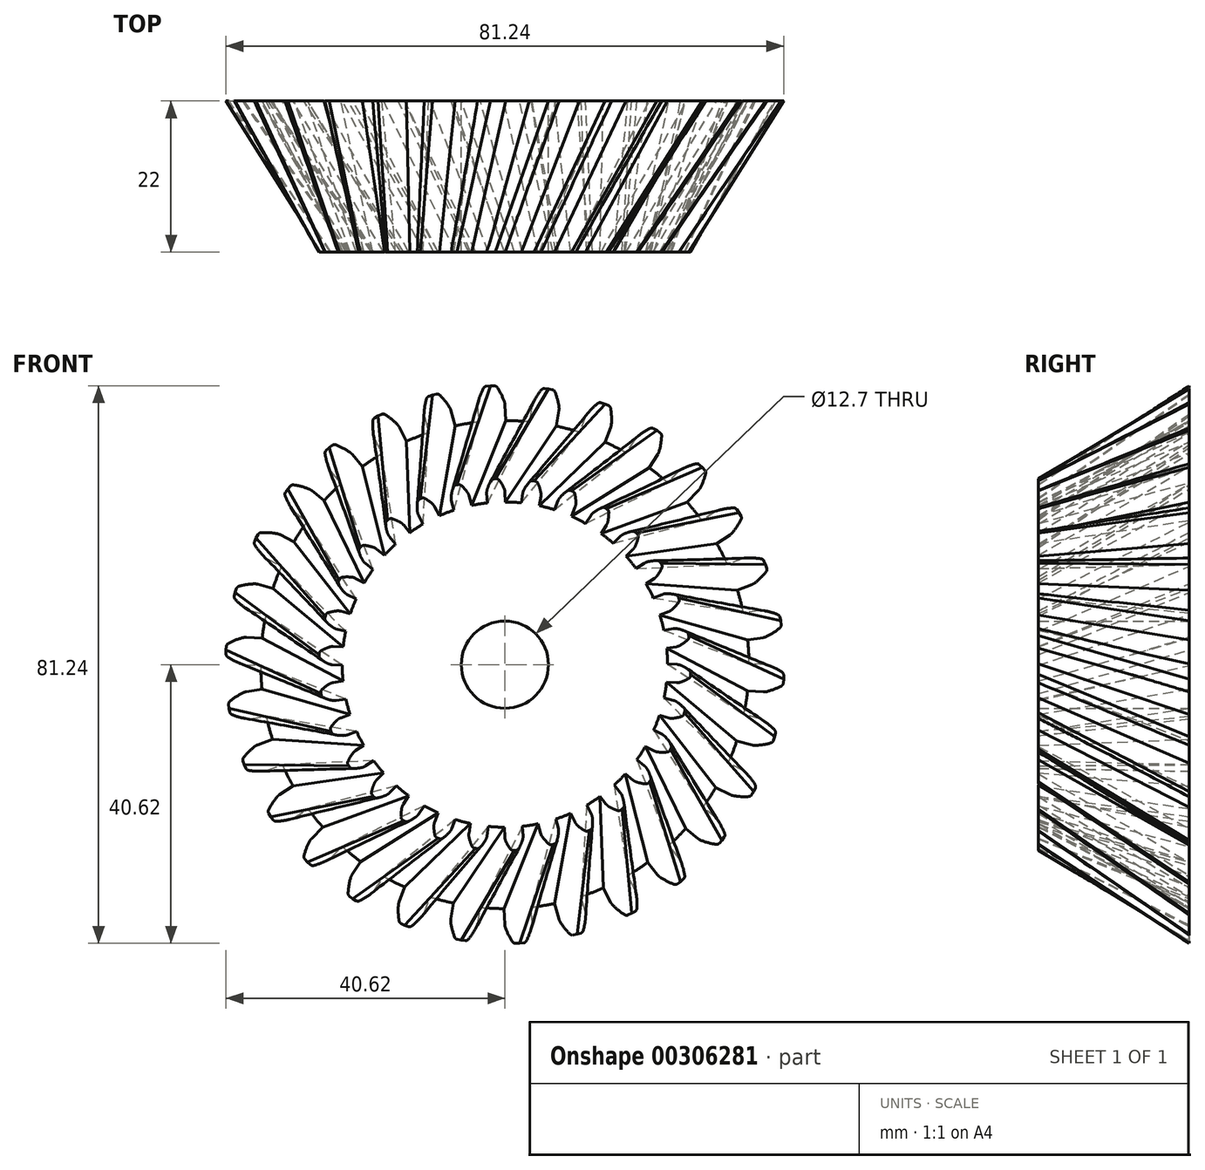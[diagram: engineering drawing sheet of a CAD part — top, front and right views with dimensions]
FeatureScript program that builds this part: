
annotation { "Feature Type Name" : "Feature", "Feature Type Description" : "" }
export const myFeature = defineFeature(function(context is Context, id is Id, definition is map)
    precondition{}
    {
        {
            var Q0;
            Q0=qCreatedBy(makeId("Front.planeOp"),FACE);
            cPlane(context, id + "F0", {"entities" : qUnion([Q0]), "cplaneType" : CPlaneType.OFFSET, "offset" : 22 * mm, "width" : 152.4 * mm, "height" : 152.4 * mm});
        }
        {
            var Q0;
            Q0=qCreatedBy(makeId("Front.planeOp"),FACE);
            var sketch = newSketch(context, id + "F1", { "sketchPlane" : qUnion([Q0])});
            skArc(sketch, "E0", {"start": v(-3.85, 35.35) * mm, "mid": v(-5.56, 35.12) * mm, "end": v(-7.26, 34.81) * mm});
            skArc(sketch, "E1.trimOffspring", {"start": v(-0.08, 38.33) * mm, "mid": v(-0.54, 39.4) * mm, "end": v(-1.12, 40.4) * mm});
            skLineSegment(sketch, "E2", {"start": v(-1.54, 40.62) * mm, "end": v(-2.13, 40.62) * mm});
            skLineSegment(sketch, "E3", {"start": v(0.01, 37.88) * mm, "end": v(0.13, 35.56) * mm});
            skLineSegment(sketch, "E4.MirrorCS", {"start": v(-2.7, 40.56) * mm, "end": v(-2.13, 40.62) * mm});
            skArc(sketch, "E5.MirrorCS", {"start": v(-3.93, 38.13) * mm, "mid": v(-3.58, 39.24) * mm, "end": v(-3.1, 40.3) * mm});
            skLineSegment(sketch, "E6.MirrorCS", {"start": v(-3.97, 37.67) * mm, "end": v(-3.85, 35.35) * mm});
            skPoint(sketch, "E7.visualSharp", {"position": v(-2.98, 40.53) * mm});
            skArc(sketch, "E7.filletArc", {"start": v(-2.7, 40.56) * mm, "mid": v(-2.94, 40.47) * mm, "end": v(-3.1, 40.3) * mm});
            skPoint(sketch, "E8.visualSharp", {"position": v(-1.28, 40.62) * mm});
            skArc(sketch, "E8.filletArc", {"start": v(-1.12, 40.4) * mm, "mid": v(-1.3, 40.56) * mm, "end": v(-1.54, 40.62) * mm});
            skPoint(sketch, "E9.visualSharp", {"position": v(-3.98, 37.9) * mm});
            skArc(sketch, "E9.filletArc", {"start": v(-3.93, 38.13) * mm, "mid": v(-3.97, 37.9) * mm, "end": v(-3.97, 37.67) * mm});
            skPoint(sketch, "E10.visualSharp", {"position": v(0, 38.1) * mm});
            skArc(sketch, "E10.filletArc", {"start": v(0.01, 37.88) * mm, "mid": v(-0.02, 38.1) * mm, "end": v(-0.08, 38.33) * mm});
            skLineSegment(sketch, "E11.1.0", {"start": v(-11.72, 36.02) * mm, "end": v(-11.12, 33.78) * mm});
            skPoint(sketch, "E11.1.1", {"position": v(-11.77, 36.24) * mm});
            skArc(sketch, "E11.1.2", {"start": v(-8.05, 37.48) * mm, "mid": v(-8.72, 38.42) * mm, "end": v(-9.5, 39.28) * mm});
            skArc(sketch, "E11.1.3", {"start": v(-11.77, 36.48) * mm, "mid": v(-11.66, 37.63) * mm, "end": v(-11.42, 38.76) * mm});
            skLineSegment(sketch, "E11.1.4", {"start": v(-9.96, 39.41) * mm, "end": v(-10.53, 39.29) * mm});
            skPoint(sketch, "E11.1.5", {"position": v(-11.34, 39.03) * mm});
            skPoint(sketch, "E11.1.6", {"position": v(-9.7, 39.47) * mm});
            skPoint(sketch, "E11.1.7", {"position": v(-7.92, 37.27) * mm});
            skLineSegment(sketch, "E11.1.8", {"start": v(-7.86, 37.05) * mm, "end": v(-7.26, 34.81) * mm});
            skLineSegment(sketch, "E11.1.9", {"start": v(-11.08, 39.1) * mm, "end": v(-10.53, 39.29) * mm});
            skArc(sketch, "E11.1.10", {"start": v(-11.08, 39.1) * mm, "mid": v(-11.3, 38.98) * mm, "end": v(-11.42, 38.76) * mm});
            skArc(sketch, "E11.1.11", {"start": v(-9.5, 39.28) * mm, "mid": v(-9.7, 39.4) * mm, "end": v(-9.96, 39.41) * mm});
            skArc(sketch, "E11.1.12", {"start": v(-11.77, 36.48) * mm, "mid": v(-11.76, 36.25) * mm, "end": v(-11.72, 36.02) * mm});
            skArc(sketch, "E11.1.13", {"start": v(-7.86, 37.05) * mm, "mid": v(-7.94, 37.27) * mm, "end": v(-8.05, 37.48) * mm});
            skLineSegment(sketch, "E11.2.0", {"start": v(-18.95, 32.8) * mm, "end": v(-17.9, 30.73) * mm});
            skPoint(sketch, "E11.2.1", {"position": v(-19.05, 33) * mm});
            skArc(sketch, "E11.2.2", {"start": v(-15.66, 34.99) * mm, "mid": v(-16.52, 35.77) * mm, "end": v(-17.45, 36.45) * mm});
            skArc(sketch, "E11.2.3", {"start": v(-19.1, 33.24) * mm, "mid": v(-19.23, 34.39) * mm, "end": v(-19.23, 35.54) * mm});
            skLineSegment(sketch, "E11.2.4", {"start": v(-17.93, 36.48) * mm, "end": v(-18.47, 36.24) * mm});
            skPoint(sketch, "E11.2.5", {"position": v(-19.2, 35.82) * mm});
            skPoint(sketch, "E11.2.6", {"position": v(-17.69, 36.59) * mm});
            skPoint(sketch, "E11.2.7", {"position": v(-15.5, 34.8) * mm});
            skLineSegment(sketch, "E11.2.8", {"start": v(-15.4, 34.6) * mm, "end": v(-14.34, 32.54) * mm});
            skLineSegment(sketch, "E11.2.9", {"start": v(-18.97, 35.95) * mm, "end": v(-18.47, 36.24) * mm});
            skArc(sketch, "E11.2.10", {"start": v(-18.97, 35.95) * mm, "mid": v(-19.15, 35.78) * mm, "end": v(-19.23, 35.54) * mm});
            skArc(sketch, "E11.2.11", {"start": v(-17.45, 36.45) * mm, "mid": v(-17.69, 36.52) * mm, "end": v(-17.93, 36.48) * mm});
            skArc(sketch, "E11.2.12", {"start": v(-19.1, 33.24) * mm, "mid": v(-19.04, 33.01) * mm, "end": v(-18.95, 32.8) * mm});
            skArc(sketch, "E11.2.13", {"start": v(-15.4, 34.6) * mm, "mid": v(-15.52, 34.8) * mm, "end": v(-15.66, 34.99) * mm});
            skLineSegment(sketch, "E11.3.0", {"start": v(-25.35, 28.14) * mm, "end": v(-23.9, 26.34) * mm});
            skPoint(sketch, "E11.3.1", {"position": v(-25.5, 28.31) * mm});
            skArc(sketch, "E11.3.2", {"start": v(-22.6, 30.96) * mm, "mid": v(-23.6, 31.55) * mm, "end": v(-24.65, 32.02) * mm});
            skArc(sketch, "E11.3.3", {"start": v(-25.59, 28.54) * mm, "mid": v(-25.96, 29.64) * mm, "end": v(-26.2, 30.77) * mm});
            skLineSegment(sketch, "E11.3.4", {"start": v(-25.13, 31.95) * mm, "end": v(-25.6, 31.61) * mm});
            skPoint(sketch, "E11.3.5", {"position": v(-26.23, 31.04) * mm});
            skPoint(sketch, "E11.3.6", {"position": v(-24.9, 32.11) * mm});
            skPoint(sketch, "E11.3.7", {"position": v(-22.4, 30.82) * mm});
            skLineSegment(sketch, "E11.3.8", {"start": v(-22.25, 30.65) * mm, "end": v(-20.8, 28.85) * mm});
            skLineSegment(sketch, "E11.3.9", {"start": v(-26.03, 31.22) * mm, "end": v(-25.6, 31.61) * mm});
            skArc(sketch, "E11.3.10", {"start": v(-26.03, 31.22) * mm, "mid": v(-26.17, 31.02) * mm, "end": v(-26.2, 30.77) * mm});
            skArc(sketch, "E11.3.11", {"start": v(-24.65, 32.02) * mm, "mid": v(-24.9, 32.05) * mm, "end": v(-25.13, 31.95) * mm});
            skArc(sketch, "E11.3.12", {"start": v(-25.59, 28.54) * mm, "mid": v(-25.49, 28.33) * mm, "end": v(-25.35, 28.14) * mm});
            skArc(sketch, "E11.3.13", {"start": v(-22.25, 30.65) * mm, "mid": v(-22.41, 30.82) * mm, "end": v(-22.6, 30.96) * mm});
            skLineSegment(sketch, "E11.4.0", {"start": v(-30.65, 22.25) * mm, "end": v(-28.85, 20.8) * mm});
            skPoint(sketch, "E11.4.1", {"position": v(-30.82, 22.4) * mm});
            skArc(sketch, "E11.4.2", {"start": v(-28.54, 25.59) * mm, "mid": v(-29.64, 25.96) * mm, "end": v(-30.77, 26.2) * mm});
            skArc(sketch, "E11.4.3", {"start": v(-30.96, 22.6) * mm, "mid": v(-31.55, 23.6) * mm, "end": v(-32.02, 24.65) * mm});
            skLineSegment(sketch, "E11.4.4", {"start": v(-31.22, 26.03) * mm, "end": v(-31.61, 25.6) * mm});
            skPoint(sketch, "E11.4.5", {"position": v(-32.11, 24.9) * mm});
            skPoint(sketch, "E11.4.6", {"position": v(-31.04, 26.23) * mm});
            skPoint(sketch, "E11.4.7", {"position": v(-28.31, 25.5) * mm});
            skLineSegment(sketch, "E11.4.8", {"start": v(-28.14, 25.35) * mm, "end": v(-26.34, 23.9) * mm});
            skLineSegment(sketch, "E11.4.9", {"start": v(-31.95, 25.13) * mm, "end": v(-31.61, 25.6) * mm});
            skArc(sketch, "E11.4.10", {"start": v(-31.95, 25.13) * mm, "mid": v(-32.05, 24.9) * mm, "end": v(-32.02, 24.65) * mm});
            skArc(sketch, "E11.4.11", {"start": v(-30.77, 26.2) * mm, "mid": v(-31.02, 26.17) * mm, "end": v(-31.22, 26.03) * mm});
            skArc(sketch, "E11.4.12", {"start": v(-30.96, 22.6) * mm, "mid": v(-30.82, 22.41) * mm, "end": v(-30.65, 22.25) * mm});
            skArc(sketch, "E11.4.13", {"start": v(-28.14, 25.35) * mm, "mid": v(-28.33, 25.49) * mm, "end": v(-28.54, 25.59) * mm});
            skLineSegment(sketch, "E11.5.0", {"start": v(-34.6, 15.4) * mm, "end": v(-32.54, 14.34) * mm});
            skPoint(sketch, "E11.5.1", {"position": v(-34.8, 15.5) * mm});
            skArc(sketch, "E11.5.2", {"start": v(-33.24, 19.1) * mm, "mid": v(-34.39, 19.23) * mm, "end": v(-35.54, 19.23) * mm});
            skArc(sketch, "E11.5.3", {"start": v(-34.99, 15.66) * mm, "mid": v(-35.77, 16.52) * mm, "end": v(-36.45, 17.45) * mm});
            skLineSegment(sketch, "E11.5.4", {"start": v(-35.95, 18.97) * mm, "end": v(-36.24, 18.47) * mm});
            skPoint(sketch, "E11.5.5", {"position": v(-36.59, 17.69) * mm});
            skPoint(sketch, "E11.5.6", {"position": v(-35.82, 19.2) * mm});
            skPoint(sketch, "E11.5.7", {"position": v(-33, 19.05) * mm});
            skLineSegment(sketch, "E11.5.8", {"start": v(-32.8, 18.95) * mm, "end": v(-30.73, 17.9) * mm});
            skLineSegment(sketch, "E11.5.9", {"start": v(-36.48, 17.93) * mm, "end": v(-36.24, 18.47) * mm});
            skArc(sketch, "E11.5.10", {"start": v(-36.48, 17.93) * mm, "mid": v(-36.52, 17.69) * mm, "end": v(-36.45, 17.45) * mm});
            skArc(sketch, "E11.5.11", {"start": v(-35.54, 19.23) * mm, "mid": v(-35.78, 19.15) * mm, "end": v(-35.95, 18.97) * mm});
            skArc(sketch, "E11.5.12", {"start": v(-34.99, 15.66) * mm, "mid": v(-34.8, 15.52) * mm, "end": v(-34.6, 15.4) * mm});
            skArc(sketch, "E11.5.13", {"start": v(-32.8, 18.95) * mm, "mid": v(-33.01, 19.04) * mm, "end": v(-33.24, 19.1) * mm});
            skLineSegment(sketch, "E11.6.0", {"start": v(-37.05, 7.86) * mm, "end": v(-34.81, 7.26) * mm});
            skPoint(sketch, "E11.6.1", {"position": v(-37.27, 7.92) * mm});
            skArc(sketch, "E11.6.2", {"start": v(-36.48, 11.77) * mm, "mid": v(-37.63, 11.66) * mm, "end": v(-38.76, 11.42) * mm});
            skArc(sketch, "E11.6.3", {"start": v(-37.48, 8.05) * mm, "mid": v(-38.42, 8.72) * mm, "end": v(-39.28, 9.5) * mm});
            skLineSegment(sketch, "E11.6.4", {"start": v(-39.1, 11.08) * mm, "end": v(-39.29, 10.53) * mm});
            skPoint(sketch, "E11.6.5", {"position": v(-39.47, 9.7) * mm});
            skPoint(sketch, "E11.6.6", {"position": v(-39.03, 11.34) * mm});
            skPoint(sketch, "E11.6.7", {"position": v(-36.24, 11.77) * mm});
            skLineSegment(sketch, "E11.6.8", {"start": v(-36.02, 11.72) * mm, "end": v(-33.78, 11.12) * mm});
            skLineSegment(sketch, "E11.6.9", {"start": v(-39.41, 9.96) * mm, "end": v(-39.29, 10.53) * mm});
            skArc(sketch, "E11.6.10", {"start": v(-39.41, 9.96) * mm, "mid": v(-39.4, 9.7) * mm, "end": v(-39.28, 9.5) * mm});
            skArc(sketch, "E11.6.11", {"start": v(-38.76, 11.42) * mm, "mid": v(-38.98, 11.3) * mm, "end": v(-39.1, 11.08) * mm});
            skArc(sketch, "E11.6.12", {"start": v(-37.48, 8.05) * mm, "mid": v(-37.27, 7.94) * mm, "end": v(-37.05, 7.86) * mm});
            skArc(sketch, "E11.6.13", {"start": v(-36.02, 11.72) * mm, "mid": v(-36.25, 11.76) * mm, "end": v(-36.48, 11.77) * mm});
            skLineSegment(sketch, "E11.7.0", {"start": v(-37.88, -0.01) * mm, "end": v(-35.56, -0.13) * mm});
            skPoint(sketch, "E11.7.1", {"position": v(-38.1, 0) * mm});
            skArc(sketch, "E11.7.2", {"start": v(-38.13, 3.93) * mm, "mid": v(-39.24, 3.58) * mm, "end": v(-40.3, 3.1) * mm});
            skArc(sketch, "E11.7.3", {"start": v(-38.33, 0.08) * mm, "mid": v(-39.4, 0.54) * mm, "end": v(-40.4, 1.12) * mm});
            skLineSegment(sketch, "E11.7.4", {"start": v(-40.56, 2.7) * mm, "end": v(-40.62, 2.13) * mm});
            skPoint(sketch, "E11.7.5", {"position": v(-40.62, 1.28) * mm});
            skPoint(sketch, "E11.7.6", {"position": v(-40.53, 2.98) * mm});
            skPoint(sketch, "E11.7.7", {"position": v(-37.9, 3.98) * mm});
            skLineSegment(sketch, "E11.7.8", {"start": v(-37.67, 3.97) * mm, "end": v(-35.35, 3.85) * mm});
            skLineSegment(sketch, "E11.7.9", {"start": v(-40.62, 1.54) * mm, "end": v(-40.62, 2.13) * mm});
            skArc(sketch, "E11.7.10", {"start": v(-40.62, 1.54) * mm, "mid": v(-40.56, 1.3) * mm, "end": v(-40.4, 1.12) * mm});
            skArc(sketch, "E11.7.11", {"start": v(-40.3, 3.1) * mm, "mid": v(-40.47, 2.94) * mm, "end": v(-40.56, 2.7) * mm});
            skArc(sketch, "E11.7.12", {"start": v(-38.33, 0.08) * mm, "mid": v(-38.1, 0.02) * mm, "end": v(-37.88, -0.01) * mm});
            skArc(sketch, "E11.7.13", {"start": v(-37.67, 3.97) * mm, "mid": v(-37.9, 3.97) * mm, "end": v(-38.13, 3.93) * mm});
            skLineSegment(sketch, "E11.8.0", {"start": v(-37.05, -7.89) * mm, "end": v(-34.76, -7.52) * mm});
            skPoint(sketch, "E11.8.1", {"position": v(-37.27, -7.92) * mm});
            skArc(sketch, "E11.8.2", {"start": v(-38.11, -4.09) * mm, "mid": v(-39.12, -4.65) * mm, "end": v(-40.06, -5.34) * mm});
            skArc(sketch, "E11.8.3", {"start": v(-37.51, -7.9) * mm, "mid": v(-38.65, -7.66) * mm, "end": v(-39.74, -7.3) * mm});
            skLineSegment(sketch, "E11.8.4", {"start": v(-40.24, -5.78) * mm, "end": v(-40.17, -6.36) * mm});
            skPoint(sketch, "E11.8.5", {"position": v(-40, -7.2) * mm});
            skPoint(sketch, "E11.8.6", {"position": v(-40.26, -5.52) * mm});
            skPoint(sketch, "E11.8.7", {"position": v(-37.9, -3.98) * mm});
            skLineSegment(sketch, "E11.8.8", {"start": v(-37.67, -3.95) * mm, "end": v(-35.38, -3.58) * mm});
            skLineSegment(sketch, "E11.8.9", {"start": v(-40.05, -6.93) * mm, "end": v(-40.17, -6.36) * mm});
            skArc(sketch, "E11.8.10", {"start": v(-40.05, -6.93) * mm, "mid": v(-39.94, -7.16) * mm, "end": v(-39.74, -7.3) * mm});
            skArc(sketch, "E11.8.11", {"start": v(-40.06, -5.34) * mm, "mid": v(-40.2, -5.54) * mm, "end": v(-40.24, -5.78) * mm});
            skArc(sketch, "E11.8.12", {"start": v(-37.51, -7.9) * mm, "mid": v(-37.28, -7.9) * mm, "end": v(-37.05, -7.89) * mm});
            skArc(sketch, "E11.8.13", {"start": v(-37.67, -3.95) * mm, "mid": v(-37.9, -4) * mm, "end": v(-38.11, -4.09) * mm});
            skLineSegment(sketch, "E11.9.0", {"start": v(-34.6, -15.42) * mm, "end": v(-32.43, -14.59) * mm});
            skPoint(sketch, "E11.9.1", {"position": v(-34.8, -15.5) * mm});
            skArc(sketch, "E11.9.2", {"start": v(-36.43, -11.92) * mm, "mid": v(-37.3, -12.69) * mm, "end": v(-38.07, -13.55) * mm});
            skArc(sketch, "E11.9.3", {"start": v(-35.05, -15.52) * mm, "mid": v(-36.2, -15.53) * mm, "end": v(-37.36, -15.4) * mm});
            skLineSegment(sketch, "E11.9.4", {"start": v(-38.15, -14.02) * mm, "end": v(-37.97, -14.58) * mm});
            skPoint(sketch, "E11.9.5", {"position": v(-37.63, -15.35) * mm});
            skPoint(sketch, "E11.9.6", {"position": v(-38.24, -13.77) * mm});
            skPoint(sketch, "E11.9.7", {"position": v(-36.24, -11.77) * mm});
            skLineSegment(sketch, "E11.9.8", {"start": v(-36.03, -11.7) * mm, "end": v(-33.86, -10.86) * mm});
            skLineSegment(sketch, "E11.9.9", {"start": v(-37.74, -15.11) * mm, "end": v(-37.97, -14.58) * mm});
            skArc(sketch, "E11.9.10", {"start": v(-37.74, -15.11) * mm, "mid": v(-37.58, -15.3) * mm, "end": v(-37.36, -15.4) * mm});
            skArc(sketch, "E11.9.11", {"start": v(-38.07, -13.55) * mm, "mid": v(-38.17, -13.77) * mm, "end": v(-38.15, -14.02) * mm});
            skArc(sketch, "E11.9.12", {"start": v(-35.05, -15.52) * mm, "mid": v(-34.82, -15.48) * mm, "end": v(-34.6, -15.42) * mm});
            skArc(sketch, "E11.9.13", {"start": v(-36.03, -11.7) * mm, "mid": v(-36.24, -11.8) * mm, "end": v(-36.43, -11.92) * mm});
            skLineSegment(sketch, "E11.10.0", {"start": v(-30.64, -22.27) * mm, "end": v(-28.7, -21) * mm});
            skPoint(sketch, "E11.10.1", {"position": v(-30.82, -22.4) * mm});
            skArc(sketch, "E11.10.2", {"start": v(-33.16, -19.24) * mm, "mid": v(-33.85, -20.16) * mm, "end": v(-34.42, -21.17) * mm});
            skArc(sketch, "E11.10.3", {"start": v(-31.06, -22.47) * mm, "mid": v(-32.19, -22.72) * mm, "end": v(-33.34, -22.84) * mm});
            skLineSegment(sketch, "E11.10.4", {"start": v(-34.4, -21.65) * mm, "end": v(-34.11, -22.15) * mm});
            skPoint(sketch, "E11.10.5", {"position": v(-33.61, -22.84) * mm});
            skPoint(sketch, "E11.10.6", {"position": v(-34.54, -21.42) * mm});
            skPoint(sketch, "E11.10.7", {"position": v(-33, -19.05) * mm});
            skLineSegment(sketch, "E11.10.8", {"start": v(-32.8, -18.93) * mm, "end": v(-30.86, -17.66) * mm});
            skLineSegment(sketch, "E11.10.9", {"start": v(-33.77, -22.63) * mm, "end": v(-34.11, -22.15) * mm});
            skArc(sketch, "E11.10.10", {"start": v(-33.77, -22.63) * mm, "mid": v(-33.58, -22.78) * mm, "end": v(-33.34, -22.84) * mm});
            skArc(sketch, "E11.10.11", {"start": v(-34.42, -21.17) * mm, "mid": v(-34.47, -21.41) * mm, "end": v(-34.4, -21.65) * mm});
            skArc(sketch, "E11.10.12", {"start": v(-31.06, -22.47) * mm, "mid": v(-30.84, -22.38) * mm, "end": v(-30.64, -22.27) * mm});
            skArc(sketch, "E11.10.13", {"start": v(-32.8, -18.93) * mm, "mid": v(-33, -19.07) * mm, "end": v(-33.16, -19.24) * mm});
            skLineSegment(sketch, "E11.11.0", {"start": v(-25.34, -28.16) * mm, "end": v(-23.7, -26.52) * mm});
            skPoint(sketch, "E11.11.1", {"position": v(-25.5, -28.31) * mm});
            skArc(sketch, "E11.11.2", {"start": v(-28.43, -25.7) * mm, "mid": v(-28.92, -26.76) * mm, "end": v(-29.27, -27.86) * mm});
            skArc(sketch, "E11.11.3", {"start": v(-25.7, -28.43) * mm, "mid": v(-26.76, -28.92) * mm, "end": v(-27.86, -29.27) * mm});
            skLineSegment(sketch, "E11.11.4", {"start": v(-29.15, -28.33) * mm, "end": v(-28.76, -28.76) * mm});
            skPoint(sketch, "E11.11.5", {"position": v(-28.13, -29.33) * mm});
            skPoint(sketch, "E11.11.6", {"position": v(-29.33, -28.13) * mm});
            skPoint(sketch, "E11.11.7", {"position": v(-28.31, -25.5) * mm});
            skLineSegment(sketch, "E11.11.8", {"start": v(-28.16, -25.34) * mm, "end": v(-26.52, -23.7) * mm});
            skLineSegment(sketch, "E11.11.9", {"start": v(-28.33, -29.15) * mm, "end": v(-28.76, -28.76) * mm});
            skArc(sketch, "E11.11.10", {"start": v(-28.33, -29.15) * mm, "mid": v(-28.1, -29.27) * mm, "end": v(-27.86, -29.27) * mm});
            skArc(sketch, "E11.11.11", {"start": v(-29.27, -27.86) * mm, "mid": v(-29.27, -28.1) * mm, "end": v(-29.15, -28.33) * mm});
            skArc(sketch, "E11.11.12", {"start": v(-25.7, -28.43) * mm, "mid": v(-25.51, -28.3) * mm, "end": v(-25.34, -28.16) * mm});
            skArc(sketch, "E11.11.13", {"start": v(-28.16, -25.34) * mm, "mid": v(-28.3, -25.51) * mm, "end": v(-28.43, -25.7) * mm});
            skLineSegment(sketch, "E11.12.0", {"start": v(-18.93, -32.8) * mm, "end": v(-17.66, -30.86) * mm});
            skPoint(sketch, "E11.12.1", {"position": v(-19.05, -33) * mm});
            skArc(sketch, "E11.12.2", {"start": v(-22.47, -31.06) * mm, "mid": v(-22.72, -32.19) * mm, "end": v(-22.84, -33.34) * mm});
            skArc(sketch, "E11.12.3", {"start": v(-19.24, -33.16) * mm, "mid": v(-20.16, -33.85) * mm, "end": v(-21.17, -34.42) * mm});
            skLineSegment(sketch, "E11.12.4", {"start": v(-22.63, -33.77) * mm, "end": v(-22.15, -34.11) * mm});
            skPoint(sketch, "E11.12.5", {"position": v(-21.42, -34.54) * mm});
            skPoint(sketch, "E11.12.6", {"position": v(-22.84, -33.61) * mm});
            skPoint(sketch, "E11.12.7", {"position": v(-22.4, -30.82) * mm});
            skLineSegment(sketch, "E11.12.8", {"start": v(-22.27, -30.64) * mm, "end": v(-21, -28.7) * mm});
            skLineSegment(sketch, "E11.12.9", {"start": v(-21.65, -34.4) * mm, "end": v(-22.15, -34.11) * mm});
            skArc(sketch, "E11.12.10", {"start": v(-21.65, -34.4) * mm, "mid": v(-21.41, -34.47) * mm, "end": v(-21.17, -34.42) * mm});
            skArc(sketch, "E11.12.11", {"start": v(-22.84, -33.34) * mm, "mid": v(-22.78, -33.58) * mm, "end": v(-22.63, -33.77) * mm});
            skArc(sketch, "E11.12.12", {"start": v(-19.24, -33.16) * mm, "mid": v(-19.07, -33) * mm, "end": v(-18.93, -32.8) * mm});
            skArc(sketch, "E11.12.13", {"start": v(-22.27, -30.64) * mm, "mid": v(-22.38, -30.84) * mm, "end": v(-22.47, -31.06) * mm});
            skLineSegment(sketch, "E11.13.0", {"start": v(-11.7, -36.03) * mm, "end": v(-10.86, -33.86) * mm});
            skPoint(sketch, "E11.13.1", {"position": v(-11.77, -36.24) * mm});
            skArc(sketch, "E11.13.2", {"start": v(-15.52, -35.05) * mm, "mid": v(-15.53, -36.2) * mm, "end": v(-15.4, -37.36) * mm});
            skArc(sketch, "E11.13.3", {"start": v(-11.92, -36.43) * mm, "mid": v(-12.69, -37.3) * mm, "end": v(-13.55, -38.07) * mm});
            skLineSegment(sketch, "E11.13.4", {"start": v(-15.11, -37.74) * mm, "end": v(-14.58, -37.97) * mm});
            skPoint(sketch, "E11.13.5", {"position": v(-13.77, -38.24) * mm});
            skPoint(sketch, "E11.13.6", {"position": v(-15.35, -37.63) * mm});
            skPoint(sketch, "E11.13.7", {"position": v(-15.5, -34.8) * mm});
            skLineSegment(sketch, "E11.13.8", {"start": v(-15.42, -34.6) * mm, "end": v(-14.59, -32.43) * mm});
            skLineSegment(sketch, "E11.13.9", {"start": v(-14.02, -38.15) * mm, "end": v(-14.58, -37.97) * mm});
            skArc(sketch, "E11.13.10", {"start": v(-14.02, -38.15) * mm, "mid": v(-13.77, -38.17) * mm, "end": v(-13.55, -38.07) * mm});
            skArc(sketch, "E11.13.11", {"start": v(-15.4, -37.36) * mm, "mid": v(-15.3, -37.58) * mm, "end": v(-15.11, -37.74) * mm});
            skArc(sketch, "E11.13.12", {"start": v(-11.92, -36.43) * mm, "mid": v(-11.8, -36.24) * mm, "end": v(-11.7, -36.03) * mm});
            skArc(sketch, "E11.13.13", {"start": v(-15.42, -34.6) * mm, "mid": v(-15.48, -34.82) * mm, "end": v(-15.52, -35.05) * mm});
            skLineSegment(sketch, "E11.14.0", {"start": v(-3.95, -37.67) * mm, "end": v(-3.58, -35.38) * mm});
            skPoint(sketch, "E11.14.1", {"position": v(-3.98, -37.9) * mm});
            skArc(sketch, "E11.14.2", {"start": v(-7.9, -37.51) * mm, "mid": v(-7.66, -38.65) * mm, "end": v(-7.3, -39.74) * mm});
            skArc(sketch, "E11.14.3", {"start": v(-4.09, -38.11) * mm, "mid": v(-4.65, -39.12) * mm, "end": v(-5.34, -40.06) * mm});
            skLineSegment(sketch, "E11.14.4", {"start": v(-6.93, -40.05) * mm, "end": v(-6.36, -40.17) * mm});
            skPoint(sketch, "E11.14.5", {"position": v(-5.52, -40.26) * mm});
            skPoint(sketch, "E11.14.6", {"position": v(-7.2, -40) * mm});
            skPoint(sketch, "E11.14.7", {"position": v(-7.92, -37.27) * mm});
            skLineSegment(sketch, "E11.14.8", {"start": v(-7.89, -37.05) * mm, "end": v(-7.52, -34.76) * mm});
            skLineSegment(sketch, "E11.14.9", {"start": v(-5.78, -40.24) * mm, "end": v(-6.36, -40.17) * mm});
            skArc(sketch, "E11.14.10", {"start": v(-5.78, -40.24) * mm, "mid": v(-5.54, -40.2) * mm, "end": v(-5.34, -40.06) * mm});
            skArc(sketch, "E11.14.11", {"start": v(-7.3, -39.74) * mm, "mid": v(-7.16, -39.94) * mm, "end": v(-6.93, -40.05) * mm});
            skArc(sketch, "E11.14.12", {"start": v(-4.09, -38.11) * mm, "mid": v(-4, -37.9) * mm, "end": v(-3.95, -37.67) * mm});
            skArc(sketch, "E11.14.13", {"start": v(-7.89, -37.05) * mm, "mid": v(-7.9, -37.28) * mm, "end": v(-7.9, -37.51) * mm});
            skLineSegment(sketch, "E11.15.0", {"start": v(3.97, -37.67) * mm, "end": v(3.85, -35.35) * mm});
            skPoint(sketch, "E11.15.1", {"position": v(3.98, -37.9) * mm});
            skArc(sketch, "E11.15.2", {"start": v(0.08, -38.33) * mm, "mid": v(0.54, -39.4) * mm, "end": v(1.12, -40.4) * mm});
            skArc(sketch, "E11.15.3", {"start": v(3.93, -38.13) * mm, "mid": v(3.58, -39.24) * mm, "end": v(3.1, -40.3) * mm});
            skLineSegment(sketch, "E11.15.4", {"start": v(1.54, -40.62) * mm, "end": v(2.13, -40.62) * mm});
            skPoint(sketch, "E11.15.5", {"position": v(2.98, -40.53) * mm});
            skPoint(sketch, "E11.15.6", {"position": v(1.28, -40.62) * mm});
            skPoint(sketch, "E11.15.7", {"position": v(0, -38.1) * mm});
            skLineSegment(sketch, "E11.15.8", {"start": v(-0.01, -37.88) * mm, "end": v(-0.13, -35.56) * mm});
            skLineSegment(sketch, "E11.15.9", {"start": v(2.7, -40.56) * mm, "end": v(2.13, -40.62) * mm});
            skArc(sketch, "E11.15.10", {"start": v(2.7, -40.56) * mm, "mid": v(2.94, -40.47) * mm, "end": v(3.1, -40.3) * mm});
            skArc(sketch, "E11.15.11", {"start": v(1.12, -40.4) * mm, "mid": v(1.3, -40.56) * mm, "end": v(1.54, -40.62) * mm});
            skArc(sketch, "E11.15.12", {"start": v(3.93, -38.13) * mm, "mid": v(3.97, -37.9) * mm, "end": v(3.97, -37.67) * mm});
            skArc(sketch, "E11.15.13", {"start": v(-0.01, -37.88) * mm, "mid": v(0.02, -38.1) * mm, "end": v(0.08, -38.33) * mm});
            skLineSegment(sketch, "E11.16.0", {"start": v(11.72, -36.02) * mm, "end": v(11.12, -33.78) * mm});
            skPoint(sketch, "E11.16.1", {"position": v(11.77, -36.24) * mm});
            skArc(sketch, "E11.16.2", {"start": v(8.05, -37.48) * mm, "mid": v(8.72, -38.42) * mm, "end": v(9.5, -39.28) * mm});
            skArc(sketch, "E11.16.3", {"start": v(11.77, -36.48) * mm, "mid": v(11.66, -37.63) * mm, "end": v(11.42, -38.76) * mm});
            skLineSegment(sketch, "E11.16.4", {"start": v(9.96, -39.41) * mm, "end": v(10.53, -39.29) * mm});
            skPoint(sketch, "E11.16.5", {"position": v(11.34, -39.03) * mm});
            skPoint(sketch, "E11.16.6", {"position": v(9.7, -39.47) * mm});
            skPoint(sketch, "E11.16.7", {"position": v(7.92, -37.27) * mm});
            skLineSegment(sketch, "E11.16.8", {"start": v(7.86, -37.05) * mm, "end": v(7.26, -34.81) * mm});
            skLineSegment(sketch, "E11.16.9", {"start": v(11.08, -39.1) * mm, "end": v(10.53, -39.29) * mm});
            skArc(sketch, "E11.16.10", {"start": v(11.08, -39.1) * mm, "mid": v(11.3, -38.98) * mm, "end": v(11.42, -38.76) * mm});
            skArc(sketch, "E11.16.11", {"start": v(9.5, -39.28) * mm, "mid": v(9.7, -39.4) * mm, "end": v(9.96, -39.41) * mm});
            skArc(sketch, "E11.16.12", {"start": v(11.77, -36.48) * mm, "mid": v(11.76, -36.25) * mm, "end": v(11.72, -36.02) * mm});
            skArc(sketch, "E11.16.13", {"start": v(7.86, -37.05) * mm, "mid": v(7.94, -37.27) * mm, "end": v(8.05, -37.48) * mm});
            skLineSegment(sketch, "E11.17.0", {"start": v(18.95, -32.8) * mm, "end": v(17.9, -30.73) * mm});
            skPoint(sketch, "E11.17.1", {"position": v(19.05, -33) * mm});
            skArc(sketch, "E11.17.2", {"start": v(15.66, -34.99) * mm, "mid": v(16.52, -35.77) * mm, "end": v(17.45, -36.45) * mm});
            skArc(sketch, "E11.17.3", {"start": v(19.1, -33.24) * mm, "mid": v(19.23, -34.39) * mm, "end": v(19.23, -35.54) * mm});
            skLineSegment(sketch, "E11.17.4", {"start": v(17.93, -36.48) * mm, "end": v(18.47, -36.24) * mm});
            skPoint(sketch, "E11.17.5", {"position": v(19.2, -35.82) * mm});
            skPoint(sketch, "E11.17.6", {"position": v(17.69, -36.59) * mm});
            skPoint(sketch, "E11.17.7", {"position": v(15.5, -34.8) * mm});
            skLineSegment(sketch, "E11.17.8", {"start": v(15.4, -34.6) * mm, "end": v(14.34, -32.54) * mm});
            skLineSegment(sketch, "E11.17.9", {"start": v(18.97, -35.95) * mm, "end": v(18.47, -36.24) * mm});
            skArc(sketch, "E11.17.10", {"start": v(18.97, -35.95) * mm, "mid": v(19.15, -35.78) * mm, "end": v(19.23, -35.54) * mm});
            skArc(sketch, "E11.17.11", {"start": v(17.45, -36.45) * mm, "mid": v(17.69, -36.52) * mm, "end": v(17.93, -36.48) * mm});
            skArc(sketch, "E11.17.12", {"start": v(19.1, -33.24) * mm, "mid": v(19.04, -33.01) * mm, "end": v(18.95, -32.8) * mm});
            skArc(sketch, "E11.17.13", {"start": v(15.4, -34.6) * mm, "mid": v(15.52, -34.8) * mm, "end": v(15.66, -34.99) * mm});
            skLineSegment(sketch, "E11.18.0", {"start": v(25.35, -28.14) * mm, "end": v(23.9, -26.34) * mm});
            skPoint(sketch, "E11.18.1", {"position": v(25.5, -28.31) * mm});
            skArc(sketch, "E11.18.2", {"start": v(22.6, -30.96) * mm, "mid": v(23.6, -31.55) * mm, "end": v(24.65, -32.02) * mm});
            skArc(sketch, "E11.18.3", {"start": v(25.59, -28.54) * mm, "mid": v(25.96, -29.64) * mm, "end": v(26.2, -30.77) * mm});
            skLineSegment(sketch, "E11.18.4", {"start": v(25.13, -31.95) * mm, "end": v(25.6, -31.61) * mm});
            skPoint(sketch, "E11.18.5", {"position": v(26.23, -31.04) * mm});
            skPoint(sketch, "E11.18.6", {"position": v(24.9, -32.11) * mm});
            skPoint(sketch, "E11.18.7", {"position": v(22.4, -30.82) * mm});
            skLineSegment(sketch, "E11.18.8", {"start": v(22.25, -30.65) * mm, "end": v(20.8, -28.85) * mm});
            skLineSegment(sketch, "E11.18.9", {"start": v(26.03, -31.22) * mm, "end": v(25.6, -31.61) * mm});
            skArc(sketch, "E11.18.10", {"start": v(26.03, -31.22) * mm, "mid": v(26.17, -31.02) * mm, "end": v(26.2, -30.77) * mm});
            skArc(sketch, "E11.18.11", {"start": v(24.65, -32.02) * mm, "mid": v(24.9, -32.05) * mm, "end": v(25.13, -31.95) * mm});
            skArc(sketch, "E11.18.12", {"start": v(25.59, -28.54) * mm, "mid": v(25.49, -28.33) * mm, "end": v(25.35, -28.14) * mm});
            skArc(sketch, "E11.18.13", {"start": v(22.25, -30.65) * mm, "mid": v(22.41, -30.82) * mm, "end": v(22.6, -30.96) * mm});
            skLineSegment(sketch, "E11.19.0", {"start": v(30.65, -22.25) * mm, "end": v(28.85, -20.8) * mm});
            skPoint(sketch, "E11.19.1", {"position": v(30.82, -22.4) * mm});
            skArc(sketch, "E11.19.2", {"start": v(28.54, -25.59) * mm, "mid": v(29.64, -25.96) * mm, "end": v(30.77, -26.2) * mm});
            skArc(sketch, "E11.19.3", {"start": v(30.96, -22.6) * mm, "mid": v(31.55, -23.6) * mm, "end": v(32.02, -24.65) * mm});
            skLineSegment(sketch, "E11.19.4", {"start": v(31.22, -26.03) * mm, "end": v(31.61, -25.6) * mm});
            skPoint(sketch, "E11.19.5", {"position": v(32.11, -24.9) * mm});
            skPoint(sketch, "E11.19.6", {"position": v(31.04, -26.23) * mm});
            skPoint(sketch, "E11.19.7", {"position": v(28.31, -25.5) * mm});
            skLineSegment(sketch, "E11.19.8", {"start": v(28.14, -25.35) * mm, "end": v(26.34, -23.9) * mm});
            skLineSegment(sketch, "E11.19.9", {"start": v(31.95, -25.13) * mm, "end": v(31.61, -25.6) * mm});
            skArc(sketch, "E11.19.10", {"start": v(31.95, -25.13) * mm, "mid": v(32.05, -24.9) * mm, "end": v(32.02, -24.65) * mm});
            skArc(sketch, "E11.19.11", {"start": v(30.77, -26.2) * mm, "mid": v(31.02, -26.17) * mm, "end": v(31.22, -26.03) * mm});
            skArc(sketch, "E11.19.12", {"start": v(30.96, -22.6) * mm, "mid": v(30.82, -22.41) * mm, "end": v(30.65, -22.25) * mm});
            skArc(sketch, "E11.19.13", {"start": v(28.14, -25.35) * mm, "mid": v(28.33, -25.49) * mm, "end": v(28.54, -25.59) * mm});
            skLineSegment(sketch, "E11.20.0", {"start": v(34.6, -15.4) * mm, "end": v(32.54, -14.34) * mm});
            skPoint(sketch, "E11.20.1", {"position": v(34.8, -15.5) * mm});
            skArc(sketch, "E11.20.2", {"start": v(33.24, -19.1) * mm, "mid": v(34.39, -19.23) * mm, "end": v(35.54, -19.23) * mm});
            skArc(sketch, "E11.20.3", {"start": v(34.99, -15.66) * mm, "mid": v(35.77, -16.52) * mm, "end": v(36.45, -17.45) * mm});
            skLineSegment(sketch, "E11.20.4", {"start": v(35.95, -18.97) * mm, "end": v(36.24, -18.47) * mm});
            skPoint(sketch, "E11.20.5", {"position": v(36.59, -17.69) * mm});
            skPoint(sketch, "E11.20.6", {"position": v(35.82, -19.2) * mm});
            skPoint(sketch, "E11.20.7", {"position": v(33, -19.05) * mm});
            skLineSegment(sketch, "E11.20.8", {"start": v(32.8, -18.95) * mm, "end": v(30.73, -17.9) * mm});
            skLineSegment(sketch, "E11.20.9", {"start": v(36.48, -17.93) * mm, "end": v(36.24, -18.47) * mm});
            skArc(sketch, "E11.20.10", {"start": v(36.48, -17.93) * mm, "mid": v(36.52, -17.69) * mm, "end": v(36.45, -17.45) * mm});
            skArc(sketch, "E11.20.11", {"start": v(35.54, -19.23) * mm, "mid": v(35.78, -19.15) * mm, "end": v(35.95, -18.97) * mm});
            skArc(sketch, "E11.20.12", {"start": v(34.99, -15.66) * mm, "mid": v(34.8, -15.52) * mm, "end": v(34.6, -15.4) * mm});
            skArc(sketch, "E11.20.13", {"start": v(32.8, -18.95) * mm, "mid": v(33.01, -19.04) * mm, "end": v(33.24, -19.1) * mm});
            skLineSegment(sketch, "E11.21.0", {"start": v(37.05, -7.86) * mm, "end": v(34.81, -7.26) * mm});
            skPoint(sketch, "E11.21.1", {"position": v(37.27, -7.92) * mm});
            skArc(sketch, "E11.21.2", {"start": v(36.48, -11.77) * mm, "mid": v(37.63, -11.66) * mm, "end": v(38.76, -11.42) * mm});
            skArc(sketch, "E11.21.3", {"start": v(37.48, -8.05) * mm, "mid": v(38.42, -8.72) * mm, "end": v(39.28, -9.5) * mm});
            skLineSegment(sketch, "E11.21.4", {"start": v(39.1, -11.08) * mm, "end": v(39.29, -10.53) * mm});
            skPoint(sketch, "E11.21.5", {"position": v(39.47, -9.7) * mm});
            skPoint(sketch, "E11.21.6", {"position": v(39.03, -11.34) * mm});
            skPoint(sketch, "E11.21.7", {"position": v(36.24, -11.77) * mm});
            skLineSegment(sketch, "E11.21.8", {"start": v(36.02, -11.72) * mm, "end": v(33.78, -11.12) * mm});
            skLineSegment(sketch, "E11.21.9", {"start": v(39.41, -9.96) * mm, "end": v(39.29, -10.53) * mm});
            skArc(sketch, "E11.21.10", {"start": v(39.41, -9.96) * mm, "mid": v(39.4, -9.7) * mm, "end": v(39.28, -9.5) * mm});
            skArc(sketch, "E11.21.11", {"start": v(38.76, -11.42) * mm, "mid": v(38.98, -11.3) * mm, "end": v(39.1, -11.08) * mm});
            skArc(sketch, "E11.21.12", {"start": v(37.48, -8.05) * mm, "mid": v(37.27, -7.94) * mm, "end": v(37.05, -7.86) * mm});
            skArc(sketch, "E11.21.13", {"start": v(36.02, -11.72) * mm, "mid": v(36.25, -11.76) * mm, "end": v(36.48, -11.77) * mm});
            skLineSegment(sketch, "E11.22.0", {"start": v(37.88, 0.01) * mm, "end": v(35.56, 0.13) * mm});
            skPoint(sketch, "E11.22.1", {"position": v(38.1, 0) * mm});
            skArc(sketch, "E11.22.2", {"start": v(38.13, -3.93) * mm, "mid": v(39.24, -3.58) * mm, "end": v(40.3, -3.1) * mm});
            skArc(sketch, "E11.22.3", {"start": v(38.33, -0.08) * mm, "mid": v(39.4, -0.54) * mm, "end": v(40.4, -1.12) * mm});
            skLineSegment(sketch, "E11.22.4", {"start": v(40.56, -2.7) * mm, "end": v(40.62, -2.13) * mm});
            skPoint(sketch, "E11.22.5", {"position": v(40.62, -1.28) * mm});
            skPoint(sketch, "E11.22.6", {"position": v(40.53, -2.98) * mm});
            skPoint(sketch, "E11.22.7", {"position": v(37.9, -3.98) * mm});
            skLineSegment(sketch, "E11.22.8", {"start": v(37.67, -3.97) * mm, "end": v(35.35, -3.85) * mm});
            skLineSegment(sketch, "E11.22.9", {"start": v(40.62, -1.54) * mm, "end": v(40.62, -2.13) * mm});
            skArc(sketch, "E11.22.10", {"start": v(40.62, -1.54) * mm, "mid": v(40.56, -1.3) * mm, "end": v(40.4, -1.12) * mm});
            skArc(sketch, "E11.22.11", {"start": v(40.3, -3.1) * mm, "mid": v(40.47, -2.94) * mm, "end": v(40.56, -2.7) * mm});
            skArc(sketch, "E11.22.12", {"start": v(38.33, -0.08) * mm, "mid": v(38.1, -0.02) * mm, "end": v(37.88, 0.01) * mm});
            skArc(sketch, "E11.22.13", {"start": v(37.67, -3.97) * mm, "mid": v(37.9, -3.97) * mm, "end": v(38.13, -3.93) * mm});
            skLineSegment(sketch, "E11.23.0", {"start": v(37.05, 7.89) * mm, "end": v(34.76, 7.52) * mm});
            skPoint(sketch, "E11.23.1", {"position": v(37.27, 7.92) * mm});
            skArc(sketch, "E11.23.2", {"start": v(38.11, 4.09) * mm, "mid": v(39.12, 4.65) * mm, "end": v(40.06, 5.34) * mm});
            skArc(sketch, "E11.23.3", {"start": v(37.51, 7.9) * mm, "mid": v(38.65, 7.66) * mm, "end": v(39.74, 7.3) * mm});
            skLineSegment(sketch, "E11.23.4", {"start": v(40.24, 5.78) * mm, "end": v(40.17, 6.36) * mm});
            skPoint(sketch, "E11.23.5", {"position": v(40, 7.2) * mm});
            skPoint(sketch, "E11.23.6", {"position": v(40.26, 5.52) * mm});
            skPoint(sketch, "E11.23.7", {"position": v(37.9, 3.98) * mm});
            skLineSegment(sketch, "E11.23.8", {"start": v(37.67, 3.95) * mm, "end": v(35.38, 3.58) * mm});
            skLineSegment(sketch, "E11.23.9", {"start": v(40.05, 6.93) * mm, "end": v(40.17, 6.36) * mm});
            skArc(sketch, "E11.23.10", {"start": v(40.05, 6.93) * mm, "mid": v(39.94, 7.16) * mm, "end": v(39.74, 7.3) * mm});
            skArc(sketch, "E11.23.11", {"start": v(40.06, 5.34) * mm, "mid": v(40.2, 5.54) * mm, "end": v(40.24, 5.78) * mm});
            skArc(sketch, "E11.23.12", {"start": v(37.51, 7.9) * mm, "mid": v(37.28, 7.9) * mm, "end": v(37.05, 7.89) * mm});
            skArc(sketch, "E11.23.13", {"start": v(37.67, 3.95) * mm, "mid": v(37.9, 4) * mm, "end": v(38.11, 4.09) * mm});
            skLineSegment(sketch, "E11.24.0", {"start": v(34.6, 15.42) * mm, "end": v(32.43, 14.59) * mm});
            skPoint(sketch, "E11.24.1", {"position": v(34.8, 15.5) * mm});
            skArc(sketch, "E11.24.2", {"start": v(36.43, 11.92) * mm, "mid": v(37.3, 12.69) * mm, "end": v(38.07, 13.55) * mm});
            skArc(sketch, "E11.24.3", {"start": v(35.05, 15.52) * mm, "mid": v(36.2, 15.53) * mm, "end": v(37.36, 15.4) * mm});
            skLineSegment(sketch, "E11.24.4", {"start": v(38.15, 14.02) * mm, "end": v(37.97, 14.58) * mm});
            skPoint(sketch, "E11.24.5", {"position": v(37.63, 15.35) * mm});
            skPoint(sketch, "E11.24.6", {"position": v(38.24, 13.77) * mm});
            skPoint(sketch, "E11.24.7", {"position": v(36.24, 11.77) * mm});
            skLineSegment(sketch, "E11.24.8", {"start": v(36.03, 11.7) * mm, "end": v(33.86, 10.86) * mm});
            skLineSegment(sketch, "E11.24.9", {"start": v(37.74, 15.11) * mm, "end": v(37.97, 14.58) * mm});
            skArc(sketch, "E11.24.10", {"start": v(37.74, 15.11) * mm, "mid": v(37.58, 15.3) * mm, "end": v(37.36, 15.4) * mm});
            skArc(sketch, "E11.24.11", {"start": v(38.07, 13.55) * mm, "mid": v(38.17, 13.77) * mm, "end": v(38.15, 14.02) * mm});
            skArc(sketch, "E11.24.12", {"start": v(35.05, 15.52) * mm, "mid": v(34.82, 15.48) * mm, "end": v(34.6, 15.42) * mm});
            skArc(sketch, "E11.24.13", {"start": v(36.03, 11.7) * mm, "mid": v(36.24, 11.8) * mm, "end": v(36.43, 11.92) * mm});
            skLineSegment(sketch, "E11.25.0", {"start": v(30.64, 22.27) * mm, "end": v(28.7, 21) * mm});
            skPoint(sketch, "E11.25.1", {"position": v(30.82, 22.4) * mm});
            skArc(sketch, "E11.25.2", {"start": v(33.16, 19.24) * mm, "mid": v(33.85, 20.16) * mm, "end": v(34.42, 21.17) * mm});
            skArc(sketch, "E11.25.3", {"start": v(31.06, 22.47) * mm, "mid": v(32.19, 22.72) * mm, "end": v(33.34, 22.84) * mm});
            skLineSegment(sketch, "E11.25.4", {"start": v(34.4, 21.65) * mm, "end": v(34.11, 22.15) * mm});
            skPoint(sketch, "E11.25.5", {"position": v(33.61, 22.84) * mm});
            skPoint(sketch, "E11.25.6", {"position": v(34.54, 21.42) * mm});
            skPoint(sketch, "E11.25.7", {"position": v(33, 19.05) * mm});
            skLineSegment(sketch, "E11.25.8", {"start": v(32.8, 18.93) * mm, "end": v(30.86, 17.66) * mm});
            skLineSegment(sketch, "E11.25.9", {"start": v(33.77, 22.63) * mm, "end": v(34.11, 22.15) * mm});
            skArc(sketch, "E11.25.10", {"start": v(33.77, 22.63) * mm, "mid": v(33.58, 22.78) * mm, "end": v(33.34, 22.84) * mm});
            skArc(sketch, "E11.25.11", {"start": v(34.42, 21.17) * mm, "mid": v(34.47, 21.41) * mm, "end": v(34.4, 21.65) * mm});
            skArc(sketch, "E11.25.12", {"start": v(31.06, 22.47) * mm, "mid": v(30.84, 22.38) * mm, "end": v(30.64, 22.27) * mm});
            skArc(sketch, "E11.25.13", {"start": v(32.8, 18.93) * mm, "mid": v(33, 19.07) * mm, "end": v(33.16, 19.24) * mm});
            skLineSegment(sketch, "E11.26.0", {"start": v(25.34, 28.16) * mm, "end": v(23.7, 26.52) * mm});
            skPoint(sketch, "E11.26.1", {"position": v(25.5, 28.31) * mm});
            skArc(sketch, "E11.26.2", {"start": v(28.43, 25.7) * mm, "mid": v(28.92, 26.76) * mm, "end": v(29.27, 27.86) * mm});
            skArc(sketch, "E11.26.3", {"start": v(25.7, 28.43) * mm, "mid": v(26.76, 28.92) * mm, "end": v(27.86, 29.27) * mm});
            skLineSegment(sketch, "E11.26.4", {"start": v(29.15, 28.33) * mm, "end": v(28.76, 28.76) * mm});
            skPoint(sketch, "E11.26.5", {"position": v(28.13, 29.33) * mm});
            skPoint(sketch, "E11.26.6", {"position": v(29.33, 28.13) * mm});
            skPoint(sketch, "E11.26.7", {"position": v(28.31, 25.5) * mm});
            skLineSegment(sketch, "E11.26.8", {"start": v(28.16, 25.34) * mm, "end": v(26.52, 23.7) * mm});
            skLineSegment(sketch, "E11.26.9", {"start": v(28.33, 29.15) * mm, "end": v(28.76, 28.76) * mm});
            skArc(sketch, "E11.26.10", {"start": v(28.33, 29.15) * mm, "mid": v(28.1, 29.27) * mm, "end": v(27.86, 29.27) * mm});
            skArc(sketch, "E11.26.11", {"start": v(29.27, 27.86) * mm, "mid": v(29.27, 28.1) * mm, "end": v(29.15, 28.33) * mm});
            skArc(sketch, "E11.26.12", {"start": v(25.7, 28.43) * mm, "mid": v(25.51, 28.3) * mm, "end": v(25.34, 28.16) * mm});
            skArc(sketch, "E11.26.13", {"start": v(28.16, 25.34) * mm, "mid": v(28.3, 25.51) * mm, "end": v(28.43, 25.7) * mm});
            skLineSegment(sketch, "E11.27.0", {"start": v(18.93, 32.8) * mm, "end": v(17.66, 30.86) * mm});
            skPoint(sketch, "E11.27.1", {"position": v(19.05, 33) * mm});
            skArc(sketch, "E11.27.2", {"start": v(22.47, 31.06) * mm, "mid": v(22.72, 32.19) * mm, "end": v(22.84, 33.34) * mm});
            skArc(sketch, "E11.27.3", {"start": v(19.24, 33.16) * mm, "mid": v(20.16, 33.85) * mm, "end": v(21.17, 34.42) * mm});
            skLineSegment(sketch, "E11.27.4", {"start": v(22.63, 33.77) * mm, "end": v(22.15, 34.11) * mm});
            skPoint(sketch, "E11.27.5", {"position": v(21.42, 34.54) * mm});
            skPoint(sketch, "E11.27.6", {"position": v(22.84, 33.61) * mm});
            skPoint(sketch, "E11.27.7", {"position": v(22.4, 30.82) * mm});
            skLineSegment(sketch, "E11.27.8", {"start": v(22.27, 30.64) * mm, "end": v(21, 28.7) * mm});
            skLineSegment(sketch, "E11.27.9", {"start": v(21.65, 34.4) * mm, "end": v(22.15, 34.11) * mm});
            skArc(sketch, "E11.27.10", {"start": v(21.65, 34.4) * mm, "mid": v(21.41, 34.47) * mm, "end": v(21.17, 34.42) * mm});
            skArc(sketch, "E11.27.11", {"start": v(22.84, 33.34) * mm, "mid": v(22.78, 33.58) * mm, "end": v(22.63, 33.77) * mm});
            skArc(sketch, "E11.27.12", {"start": v(19.24, 33.16) * mm, "mid": v(19.07, 33) * mm, "end": v(18.93, 32.8) * mm});
            skArc(sketch, "E11.27.13", {"start": v(22.27, 30.64) * mm, "mid": v(22.38, 30.84) * mm, "end": v(22.47, 31.06) * mm});
            skLineSegment(sketch, "E11.28.0", {"start": v(11.7, 36.03) * mm, "end": v(10.86, 33.86) * mm});
            skPoint(sketch, "E11.28.1", {"position": v(11.77, 36.24) * mm});
            skArc(sketch, "E11.28.2", {"start": v(15.52, 35.05) * mm, "mid": v(15.53, 36.2) * mm, "end": v(15.4, 37.36) * mm});
            skArc(sketch, "E11.28.3", {"start": v(11.92, 36.43) * mm, "mid": v(12.69, 37.3) * mm, "end": v(13.55, 38.07) * mm});
            skLineSegment(sketch, "E11.28.4", {"start": v(15.11, 37.74) * mm, "end": v(14.58, 37.97) * mm});
            skPoint(sketch, "E11.28.5", {"position": v(13.77, 38.24) * mm});
            skPoint(sketch, "E11.28.6", {"position": v(15.35, 37.63) * mm});
            skPoint(sketch, "E11.28.7", {"position": v(15.5, 34.8) * mm});
            skLineSegment(sketch, "E11.28.8", {"start": v(15.42, 34.6) * mm, "end": v(14.59, 32.43) * mm});
            skLineSegment(sketch, "E11.28.9", {"start": v(14.02, 38.15) * mm, "end": v(14.58, 37.97) * mm});
            skArc(sketch, "E11.28.10", {"start": v(14.02, 38.15) * mm, "mid": v(13.77, 38.17) * mm, "end": v(13.55, 38.07) * mm});
            skArc(sketch, "E11.28.11", {"start": v(15.4, 37.36) * mm, "mid": v(15.3, 37.58) * mm, "end": v(15.11, 37.74) * mm});
            skArc(sketch, "E11.28.12", {"start": v(11.92, 36.43) * mm, "mid": v(11.8, 36.24) * mm, "end": v(11.7, 36.03) * mm});
            skArc(sketch, "E11.28.13", {"start": v(15.42, 34.6) * mm, "mid": v(15.48, 34.82) * mm, "end": v(15.52, 35.05) * mm});
            skLineSegment(sketch, "E11.29.0", {"start": v(3.95, 37.67) * mm, "end": v(3.58, 35.38) * mm});
            skPoint(sketch, "E11.29.1", {"position": v(3.98, 37.9) * mm});
            skArc(sketch, "E11.29.2", {"start": v(7.9, 37.51) * mm, "mid": v(7.66, 38.65) * mm, "end": v(7.3, 39.74) * mm});
            skArc(sketch, "E11.29.3", {"start": v(4.09, 38.11) * mm, "mid": v(4.65, 39.12) * mm, "end": v(5.34, 40.06) * mm});
            skLineSegment(sketch, "E11.29.4", {"start": v(6.93, 40.05) * mm, "end": v(6.36, 40.17) * mm});
            skPoint(sketch, "E11.29.5", {"position": v(5.52, 40.26) * mm});
            skPoint(sketch, "E11.29.6", {"position": v(7.2, 40) * mm});
            skPoint(sketch, "E11.29.7", {"position": v(7.92, 37.27) * mm});
            skLineSegment(sketch, "E11.29.8", {"start": v(7.89, 37.05) * mm, "end": v(7.52, 34.76) * mm});
            skLineSegment(sketch, "E11.29.9", {"start": v(5.78, 40.24) * mm, "end": v(6.36, 40.17) * mm});
            skArc(sketch, "E11.29.10", {"start": v(5.78, 40.24) * mm, "mid": v(5.54, 40.2) * mm, "end": v(5.34, 40.06) * mm});
            skArc(sketch, "E11.29.11", {"start": v(7.3, 39.74) * mm, "mid": v(7.16, 39.94) * mm, "end": v(6.93, 40.05) * mm});
            skArc(sketch, "E11.29.12", {"start": v(4.09, 38.11) * mm, "mid": v(4, 37.9) * mm, "end": v(3.95, 37.67) * mm});
            skArc(sketch, "E11.29.13", {"start": v(7.89, 37.05) * mm, "mid": v(7.9, 37.28) * mm, "end": v(7.9, 37.51) * mm});
            skArc(sketch, "E12.trimOffspring", {"start": v(-11.12, 33.78) * mm, "mid": v(-12.74, 33.2) * mm, "end": v(-14.34, 32.54) * mm});
            skArc(sketch, "E13.trimOffspring", {"start": v(-17.9, 30.73) * mm, "mid": v(-19.37, 29.82) * mm, "end": v(-20.8, 28.85) * mm});
            skArc(sketch, "E14.trimOffspring", {"start": v(-23.9, 26.34) * mm, "mid": v(-25.14, 25.14) * mm, "end": v(-26.34, 23.9) * mm});
            skArc(sketch, "E15.trimOffspring", {"start": v(-28.85, 20.8) * mm, "mid": v(-29.82, 19.37) * mm, "end": v(-30.73, 17.9) * mm});
            skArc(sketch, "E16.trimOffspring", {"start": v(-32.54, 14.34) * mm, "mid": v(-33.2, 12.74) * mm, "end": v(-33.78, 11.12) * mm});
            skArc(sketch, "E17.trimOffspring", {"start": v(-34.81, 7.26) * mm, "mid": v(-35.12, 5.56) * mm, "end": v(-35.35, 3.85) * mm});
            skArc(sketch, "E18.trimOffspring", {"start": v(-35.56, -0.13) * mm, "mid": v(-35.51, -1.86) * mm, "end": v(-35.38, -3.58) * mm});
            skArc(sketch, "E19.trimOffspring", {"start": v(-34.76, -7.52) * mm, "mid": v(-34.35, -9.2) * mm, "end": v(-33.86, -10.86) * mm});
            skArc(sketch, "E20.trimOffspring", {"start": v(-32.43, -14.59) * mm, "mid": v(-31.68, -16.14) * mm, "end": v(-30.86, -17.66) * mm});
            skArc(sketch, "E21.trimOffspring", {"start": v(-28.7, -21) * mm, "mid": v(-27.64, -22.38) * mm, "end": v(-26.52, -23.7) * mm});
            skArc(sketch, "E22.trimOffspring", {"start": v(-23.7, -26.52) * mm, "mid": v(-22.38, -27.64) * mm, "end": v(-21, -28.7) * mm});
            skArc(sketch, "E23.trimOffspring", {"start": v(-17.66, -30.86) * mm, "mid": v(-16.14, -31.68) * mm, "end": v(-14.59, -32.43) * mm});
            skArc(sketch, "E24.trimOffspring", {"start": v(-10.86, -33.86) * mm, "mid": v(-9.2, -34.35) * mm, "end": v(-7.52, -34.76) * mm});
            skArc(sketch, "E25.trimOffspring", {"start": v(-3.58, -35.38) * mm, "mid": v(-1.86, -35.51) * mm, "end": v(-0.13, -35.56) * mm});
            skArc(sketch, "E26.trimOffspring", {"start": v(3.85, -35.35) * mm, "mid": v(5.56, -35.12) * mm, "end": v(7.26, -34.81) * mm});
            skArc(sketch, "E27.trimOffspring", {"start": v(11.12, -33.78) * mm, "mid": v(12.74, -33.2) * mm, "end": v(14.34, -32.54) * mm});
            skArc(sketch, "E28.trimOffspring", {"start": v(17.9, -30.73) * mm, "mid": v(19.37, -29.82) * mm, "end": v(20.8, -28.85) * mm});
            skArc(sketch, "E29.trimOffspring", {"start": v(23.9, -26.34) * mm, "mid": v(25.14, -25.14) * mm, "end": v(26.34, -23.9) * mm});
            skArc(sketch, "E30.trimOffspring", {"start": v(28.85, -20.8) * mm, "mid": v(29.82, -19.37) * mm, "end": v(30.73, -17.9) * mm});
            skArc(sketch, "E31.trimOffspring", {"start": v(32.54, -14.34) * mm, "mid": v(33.2, -12.74) * mm, "end": v(33.78, -11.12) * mm});
            skArc(sketch, "E32.trimOffspring", {"start": v(34.81, -7.26) * mm, "mid": v(35.12, -5.56) * mm, "end": v(35.35, -3.85) * mm});
            skArc(sketch, "E33.trimOffspring", {"start": v(35.56, 0.13) * mm, "mid": v(35.51, 1.86) * mm, "end": v(35.38, 3.58) * mm});
            skArc(sketch, "E34.trimOffspring", {"start": v(34.76, 7.52) * mm, "mid": v(34.35, 9.2) * mm, "end": v(33.86, 10.86) * mm});
            skArc(sketch, "E35.trimOffspring", {"start": v(32.43, 14.59) * mm, "mid": v(31.68, 16.14) * mm, "end": v(30.86, 17.66) * mm});
            skArc(sketch, "E36.trimOffspring", {"start": v(28.7, 21) * mm, "mid": v(27.64, 22.38) * mm, "end": v(26.52, 23.7) * mm});
            skArc(sketch, "E37.trimOffspring", {"start": v(23.7, 26.52) * mm, "mid": v(22.38, 27.64) * mm, "end": v(21, 28.7) * mm});
            skArc(sketch, "E38.trimOffspring", {"start": v(17.66, 30.86) * mm, "mid": v(16.14, 31.68) * mm, "end": v(14.59, 32.43) * mm});
            skArc(sketch, "E39.trimOffspring", {"start": v(10.86, 33.86) * mm, "mid": v(9.2, 34.35) * mm, "end": v(7.52, 34.76) * mm});
            skArc(sketch, "E40.trimOffspring", {"start": v(3.58, 35.38) * mm, "mid": v(1.86, 35.51) * mm, "end": v(0.13, 35.56) * mm});
            skSolve(sketch);
        }
        {
            var Q0;
            Q0=qCreatedBy(id+"F0.planeOp",FACE);
            var sketch = newSketch(context, id + "F2", { "sketchPlane" : qUnion([Q0])});
            skArc(sketch, "E41", {"start": v(-2.57, 23.56) * mm, "mid": v(-3.7, 23.4) * mm, "end": v(-4.84, 23.2) * mm});
            skArc(sketch, "E42.trimOffspring", {"start": v(-0.12, 25.69) * mm, "mid": v(-0.43, 26.3) * mm, "end": v(-0.8, 26.86) * mm});
            skLineSegment(sketch, "E43", {"start": v(0.01, 25.13) * mm, "end": v(0.09, 23.7) * mm});
            skLineSegment(sketch, "E44", {"start": v(-1.2, 27.07) * mm, "end": v(-1.42, 27.07) * mm});
            skLineSegment(sketch, "E45.MirrorCS", {"start": v(-1.63, 27.05) * mm, "end": v(-1.42, 27.07) * mm});
            skArc(sketch, "E46.MirrorCS", {"start": v(-2.57, 25.56) * mm, "mid": v(-2.32, 26.2) * mm, "end": v(-2.02, 26.8) * mm});
            skLineSegment(sketch, "E47.MirrorCS", {"start": v(-2.64, 25) * mm, "end": v(-2.57, 23.56) * mm});
            skPoint(sketch, "E48.visualSharp", {"position": v(0, 25.4) * mm});
            skArc(sketch, "E48.filletArc", {"start": v(0.01, 25.13) * mm, "mid": v(-0.03, 25.42) * mm, "end": v(-0.12, 25.69) * mm});
            skPoint(sketch, "E49.visualSharp", {"position": v(-2.66, 25.26) * mm});
            skArc(sketch, "E49.filletArc", {"start": v(-2.57, 25.56) * mm, "mid": v(-2.63, 25.28) * mm, "end": v(-2.64, 25) * mm});
            skPoint(sketch, "E50.visualSharp", {"position": v(-1.88, 27.02) * mm});
            skArc(sketch, "E50.filletArc", {"start": v(-1.63, 27.05) * mm, "mid": v(-1.85, 26.97) * mm, "end": v(-2.02, 26.8) * mm});
            skPoint(sketch, "E51.visualSharp", {"position": v(-0.96, 27.07) * mm});
            skArc(sketch, "E51.filletArc", {"start": v(-0.8, 26.86) * mm, "mid": v(-0.98, 27.02) * mm, "end": v(-1.2, 27.07) * mm});
            skPoint(sketch, "E52.1.0", {"position": v(-7.46, 26.04) * mm});
            skArc(sketch, "E52.1.1", {"start": v(-5.46, 25.1) * mm, "mid": v(-5.88, 25.63) * mm, "end": v(-6.37, 26.11) * mm});
            skLineSegment(sketch, "E52.1.2", {"start": v(-5.21, 24.58) * mm, "end": v(-4.84, 23.2) * mm});
            skPoint(sketch, "E52.1.3", {"position": v(-5.28, 24.84) * mm});
            skPoint(sketch, "E52.1.4", {"position": v(-7.85, 24.16) * mm});
            skArc(sketch, "E52.1.5", {"start": v(-7.82, 24.47) * mm, "mid": v(-7.72, 25.14) * mm, "end": v(-7.54, 25.8) * mm});
            skPoint(sketch, "E52.1.6", {"position": v(-6.56, 26.28) * mm});
            skArc(sketch, "E52.1.7", {"start": v(-6.37, 26.11) * mm, "mid": v(-6.57, 26.22) * mm, "end": v(-6.8, 26.23) * mm});
            skArc(sketch, "E52.1.8", {"start": v(-7.82, 24.47) * mm, "mid": v(-7.83, 24.18) * mm, "end": v(-7.78, 23.9) * mm});
            skArc(sketch, "E52.1.9", {"start": v(-5.21, 24.58) * mm, "mid": v(-5.31, 24.85) * mm, "end": v(-5.46, 25.1) * mm});
            skLineSegment(sketch, "E52.1.10", {"start": v(-7.78, 23.9) * mm, "end": v(-7.4, 22.51) * mm});
            skArc(sketch, "E52.1.11", {"start": v(-7.22, 26.12) * mm, "mid": v(-7.42, 26) * mm, "end": v(-7.54, 25.8) * mm});
            skLineSegment(sketch, "E52.1.12", {"start": v(-6.8, 26.23) * mm, "end": v(-7.02, 26.19) * mm});
            skLineSegment(sketch, "E52.1.13", {"start": v(-7.22, 26.12) * mm, "end": v(-7.02, 26.19) * mm});
            skPoint(sketch, "E52.2.0", {"position": v(-12.7, 23.92) * mm});
            skArc(sketch, "E52.2.1", {"start": v(-10.56, 23.42) * mm, "mid": v(-11.08, 23.85) * mm, "end": v(-11.65, 24.22) * mm});
            skLineSegment(sketch, "E52.2.2", {"start": v(-10.2, 22.96) * mm, "end": v(-9.56, 21.69) * mm});
            skPoint(sketch, "E52.2.3", {"position": v(-10.33, 23.2) * mm});
            skPoint(sketch, "E52.2.4", {"position": v(-12.7, 22) * mm});
            skArc(sketch, "E52.2.5", {"start": v(-12.74, 22.3) * mm, "mid": v(-12.78, 22.98) * mm, "end": v(-12.74, 23.66) * mm});
            skPoint(sketch, "E52.2.6", {"position": v(-11.88, 24.34) * mm});
            skArc(sketch, "E52.2.7", {"start": v(-11.65, 24.22) * mm, "mid": v(-11.88, 24.28) * mm, "end": v(-12.11, 24.24) * mm});
            skArc(sketch, "E52.2.8", {"start": v(-12.74, 22.3) * mm, "mid": v(-12.68, 22.02) * mm, "end": v(-12.58, 21.76) * mm});
            skArc(sketch, "E52.2.9", {"start": v(-10.2, 22.96) * mm, "mid": v(-10.36, 23.2) * mm, "end": v(-10.56, 23.42) * mm});
            skLineSegment(sketch, "E52.2.10", {"start": v(-12.58, 21.76) * mm, "end": v(-11.93, 20.48) * mm});
            skArc(sketch, "E52.2.11", {"start": v(-12.5, 24.05) * mm, "mid": v(-12.66, 23.89) * mm, "end": v(-12.74, 23.66) * mm});
            skLineSegment(sketch, "E52.2.12", {"start": v(-12.11, 24.24) * mm, "end": v(-12.3, 24.15) * mm});
            skLineSegment(sketch, "E52.2.13", {"start": v(-12.5, 24.05) * mm, "end": v(-12.3, 24.15) * mm});
            skPoint(sketch, "E52.3.0", {"position": v(-17.4, 20.76) * mm});
            skArc(sketch, "E52.3.1", {"start": v(-15.2, 20.71) * mm, "mid": v(-15.8, 21.02) * mm, "end": v(-16.44, 21.26) * mm});
            skLineSegment(sketch, "E52.3.2", {"start": v(-14.76, 20.34) * mm, "end": v(-13.86, 19.22) * mm});
            skPoint(sketch, "E52.3.3", {"position": v(-14.93, 20.55) * mm});
            skPoint(sketch, "E52.3.4", {"position": v(-17, 18.88) * mm});
            skArc(sketch, "E52.3.5", {"start": v(-17.1, 19.17) * mm, "mid": v(-17.28, 19.83) * mm, "end": v(-17.38, 20.5) * mm});
            skPoint(sketch, "E52.3.6", {"position": v(-16.69, 21.34) * mm});
            skArc(sketch, "E52.3.7", {"start": v(-16.44, 21.26) * mm, "mid": v(-16.67, 21.28) * mm, "end": v(-16.89, 21.2) * mm});
            skArc(sketch, "E52.3.8", {"start": v(-17.1, 19.17) * mm, "mid": v(-16.99, 18.9) * mm, "end": v(-16.83, 18.67) * mm});
            skArc(sketch, "E52.3.9", {"start": v(-14.76, 20.34) * mm, "mid": v(-14.96, 20.55) * mm, "end": v(-15.2, 20.71) * mm});
            skLineSegment(sketch, "E52.3.10", {"start": v(-16.83, 18.67) * mm, "end": v(-15.92, 17.55) * mm});
            skArc(sketch, "E52.3.11", {"start": v(-17.22, 20.93) * mm, "mid": v(-17.35, 20.73) * mm, "end": v(-17.38, 20.5) * mm});
            skLineSegment(sketch, "E52.3.12", {"start": v(-16.89, 21.2) * mm, "end": v(-17.06, 21.07) * mm});
            skLineSegment(sketch, "E52.3.13", {"start": v(-17.22, 20.93) * mm, "end": v(-17.06, 21.07) * mm});
            skPoint(sketch, "E52.4.0", {"position": v(-21.34, 16.69) * mm});
            skArc(sketch, "E52.4.1", {"start": v(-19.17, 17.1) * mm, "mid": v(-19.83, 17.28) * mm, "end": v(-20.5, 17.38) * mm});
            skLineSegment(sketch, "E52.4.2", {"start": v(-18.67, 16.83) * mm, "end": v(-17.55, 15.92) * mm});
            skPoint(sketch, "E52.4.3", {"position": v(-18.88, 17) * mm});
            skPoint(sketch, "E52.4.4", {"position": v(-20.55, 14.93) * mm});
            skArc(sketch, "E52.4.5", {"start": v(-20.71, 15.2) * mm, "mid": v(-21.02, 15.8) * mm, "end": v(-21.26, 16.44) * mm});
            skPoint(sketch, "E52.4.6", {"position": v(-20.76, 17.4) * mm});
            skArc(sketch, "E52.4.7", {"start": v(-20.5, 17.38) * mm, "mid": v(-20.73, 17.35) * mm, "end": v(-20.93, 17.22) * mm});
            skArc(sketch, "E52.4.8", {"start": v(-20.71, 15.2) * mm, "mid": v(-20.55, 14.96) * mm, "end": v(-20.34, 14.76) * mm});
            skArc(sketch, "E52.4.9", {"start": v(-18.67, 16.83) * mm, "mid": v(-18.9, 16.99) * mm, "end": v(-19.17, 17.1) * mm});
            skLineSegment(sketch, "E52.4.10", {"start": v(-20.34, 14.76) * mm, "end": v(-19.22, 13.86) * mm});
            skArc(sketch, "E52.4.11", {"start": v(-21.2, 16.89) * mm, "mid": v(-21.28, 16.67) * mm, "end": v(-21.26, 16.44) * mm});
            skLineSegment(sketch, "E52.4.12", {"start": v(-20.93, 17.22) * mm, "end": v(-21.07, 17.06) * mm});
            skLineSegment(sketch, "E52.4.13", {"start": v(-21.2, 16.89) * mm, "end": v(-21.07, 17.06) * mm});
            skPoint(sketch, "E52.5.0", {"position": v(-24.34, 11.88) * mm});
            skArc(sketch, "E52.5.1", {"start": v(-22.3, 12.74) * mm, "mid": v(-22.98, 12.78) * mm, "end": v(-23.66, 12.74) * mm});
            skLineSegment(sketch, "E52.5.2", {"start": v(-21.76, 12.58) * mm, "end": v(-20.48, 11.93) * mm});
            skPoint(sketch, "E52.5.3", {"position": v(-22, 12.7) * mm});
            skPoint(sketch, "E52.5.4", {"position": v(-23.2, 10.33) * mm});
            skArc(sketch, "E52.5.5", {"start": v(-23.42, 10.56) * mm, "mid": v(-23.85, 11.08) * mm, "end": v(-24.22, 11.65) * mm});
            skPoint(sketch, "E52.5.6", {"position": v(-23.92, 12.7) * mm});
            skArc(sketch, "E52.5.7", {"start": v(-23.66, 12.74) * mm, "mid": v(-23.89, 12.66) * mm, "end": v(-24.05, 12.5) * mm});
            skArc(sketch, "E52.5.8", {"start": v(-23.42, 10.56) * mm, "mid": v(-23.2, 10.36) * mm, "end": v(-22.96, 10.2) * mm});
            skArc(sketch, "E52.5.9", {"start": v(-21.76, 12.58) * mm, "mid": v(-22.02, 12.68) * mm, "end": v(-22.3, 12.74) * mm});
            skLineSegment(sketch, "E52.5.10", {"start": v(-22.96, 10.2) * mm, "end": v(-21.69, 9.56) * mm});
            skArc(sketch, "E52.5.11", {"start": v(-24.24, 12.11) * mm, "mid": v(-24.28, 11.88) * mm, "end": v(-24.22, 11.65) * mm});
            skLineSegment(sketch, "E52.5.12", {"start": v(-24.05, 12.5) * mm, "end": v(-24.15, 12.3) * mm});
            skLineSegment(sketch, "E52.5.13", {"start": v(-24.24, 12.11) * mm, "end": v(-24.15, 12.3) * mm});
            skPoint(sketch, "E52.6.0", {"position": v(-26.28, 6.56) * mm});
            skArc(sketch, "E52.6.1", {"start": v(-24.47, 7.82) * mm, "mid": v(-25.14, 7.72) * mm, "end": v(-25.8, 7.54) * mm});
            skLineSegment(sketch, "E52.6.2", {"start": v(-23.9, 7.78) * mm, "end": v(-22.51, 7.4) * mm});
            skPoint(sketch, "E52.6.3", {"position": v(-24.16, 7.85) * mm});
            skPoint(sketch, "E52.6.4", {"position": v(-24.84, 5.28) * mm});
            skArc(sketch, "E52.6.5", {"start": v(-25.1, 5.46) * mm, "mid": v(-25.63, 5.88) * mm, "end": v(-26.11, 6.37) * mm});
            skPoint(sketch, "E52.6.6", {"position": v(-26.04, 7.46) * mm});
            skArc(sketch, "E52.6.7", {"start": v(-25.8, 7.54) * mm, "mid": v(-26, 7.42) * mm, "end": v(-26.12, 7.22) * mm});
            skArc(sketch, "E52.6.8", {"start": v(-25.1, 5.46) * mm, "mid": v(-24.85, 5.31) * mm, "end": v(-24.58, 5.21) * mm});
            skArc(sketch, "E52.6.9", {"start": v(-23.9, 7.78) * mm, "mid": v(-24.18, 7.83) * mm, "end": v(-24.47, 7.82) * mm});
            skLineSegment(sketch, "E52.6.10", {"start": v(-24.58, 5.21) * mm, "end": v(-23.2, 4.84) * mm});
            skArc(sketch, "E52.6.11", {"start": v(-26.23, 6.8) * mm, "mid": v(-26.22, 6.57) * mm, "end": v(-26.11, 6.37) * mm});
            skLineSegment(sketch, "E52.6.12", {"start": v(-26.12, 7.22) * mm, "end": v(-26.19, 7.02) * mm});
            skLineSegment(sketch, "E52.6.13", {"start": v(-26.23, 6.8) * mm, "end": v(-26.19, 7.02) * mm});
            skPoint(sketch, "E52.7.0", {"position": v(-27.07, 0.96) * mm});
            skArc(sketch, "E52.7.1", {"start": v(-25.56, 2.57) * mm, "mid": v(-26.2, 2.32) * mm, "end": v(-26.8, 2.02) * mm});
            skLineSegment(sketch, "E52.7.2", {"start": v(-25, 2.64) * mm, "end": v(-23.56, 2.57) * mm});
            skPoint(sketch, "E52.7.3", {"position": v(-25.26, 2.66) * mm});
            skPoint(sketch, "E52.7.4", {"position": v(-25.4, 0) * mm});
            skArc(sketch, "E52.7.5", {"start": v(-25.69, 0.12) * mm, "mid": v(-26.3, 0.43) * mm, "end": v(-26.86, 0.8) * mm});
            skPoint(sketch, "E52.7.6", {"position": v(-27.02, 1.88) * mm});
            skArc(sketch, "E52.7.7", {"start": v(-26.8, 2.02) * mm, "mid": v(-26.97, 1.85) * mm, "end": v(-27.05, 1.63) * mm});
            skArc(sketch, "E52.7.8", {"start": v(-25.69, 0.12) * mm, "mid": v(-25.42, 0.03) * mm, "end": v(-25.13, -0.01) * mm});
            skArc(sketch, "E52.7.9", {"start": v(-25, 2.64) * mm, "mid": v(-25.28, 2.63) * mm, "end": v(-25.56, 2.57) * mm});
            skLineSegment(sketch, "E52.7.10", {"start": v(-25.13, -0.01) * mm, "end": v(-23.7, -0.09) * mm});
            skArc(sketch, "E52.7.11", {"start": v(-27.07, 1.2) * mm, "mid": v(-27.02, 0.98) * mm, "end": v(-26.86, 0.8) * mm});
            skLineSegment(sketch, "E52.7.12", {"start": v(-27.05, 1.63) * mm, "end": v(-27.07, 1.42) * mm});
            skLineSegment(sketch, "E52.7.13", {"start": v(-27.07, 1.2) * mm, "end": v(-27.07, 1.42) * mm});
            skPoint(sketch, "E52.8.0", {"position": v(-26.68, -4.7) * mm});
            skArc(sketch, "E52.8.1", {"start": v(-25.54, -2.8) * mm, "mid": v(-26.1, -3.17) * mm, "end": v(-26.63, -3.6) * mm});
            skLineSegment(sketch, "E52.8.2", {"start": v(-25, -2.61) * mm, "end": v(-23.58, -2.39) * mm});
            skPoint(sketch, "E52.8.3", {"position": v(-25.26, -2.66) * mm});
            skPoint(sketch, "E52.8.4", {"position": v(-24.84, -5.28) * mm});
            skArc(sketch, "E52.8.5", {"start": v(-25.15, -5.22) * mm, "mid": v(-25.8, -5.05) * mm, "end": v(-26.44, -4.8) * mm});
            skPoint(sketch, "E52.8.6", {"position": v(-26.82, -3.78) * mm});
            skArc(sketch, "E52.8.7", {"start": v(-26.63, -3.6) * mm, "mid": v(-26.77, -3.8) * mm, "end": v(-26.8, -4.03) * mm});
            skArc(sketch, "E52.8.8", {"start": v(-25.15, -5.22) * mm, "mid": v(-24.87, -5.26) * mm, "end": v(-24.58, -5.24) * mm});
            skArc(sketch, "E52.8.9", {"start": v(-25, -2.61) * mm, "mid": v(-25.27, -2.68) * mm, "end": v(-25.54, -2.8) * mm});
            skLineSegment(sketch, "E52.8.10", {"start": v(-24.58, -5.24) * mm, "end": v(-23.16, -5.01) * mm});
            skArc(sketch, "E52.8.11", {"start": v(-26.73, -4.45) * mm, "mid": v(-26.63, -4.66) * mm, "end": v(-26.44, -4.8) * mm});
            skLineSegment(sketch, "E52.8.12", {"start": v(-26.8, -4.03) * mm, "end": v(-26.78, -4.24) * mm});
            skLineSegment(sketch, "E52.8.13", {"start": v(-26.73, -4.45) * mm, "end": v(-26.78, -4.24) * mm});
            skPoint(sketch, "E52.9.0", {"position": v(-25.12, -10.14) * mm});
            skArc(sketch, "E52.9.1", {"start": v(-24.4, -8.05) * mm, "mid": v(-24.88, -8.53) * mm, "end": v(-25.3, -9.06) * mm});
            skLineSegment(sketch, "E52.9.2", {"start": v(-23.9, -7.75) * mm, "end": v(-22.57, -7.24) * mm});
            skPoint(sketch, "E52.9.3", {"position": v(-24.16, -7.85) * mm});
            skPoint(sketch, "E52.9.4", {"position": v(-23.2, -10.33) * mm});
            skArc(sketch, "E52.9.5", {"start": v(-23.52, -10.34) * mm, "mid": v(-24.2, -10.3) * mm, "end": v(-24.87, -10.2) * mm});
            skPoint(sketch, "E52.9.6", {"position": v(-25.45, -9.28) * mm});
            skArc(sketch, "E52.9.7", {"start": v(-25.3, -9.06) * mm, "mid": v(-25.4, -9.28) * mm, "end": v(-25.37, -9.51) * mm});
            skArc(sketch, "E52.9.8", {"start": v(-23.52, -10.34) * mm, "mid": v(-23.23, -10.31) * mm, "end": v(-22.95, -10.23) * mm});
            skArc(sketch, "E52.9.9", {"start": v(-23.9, -7.75) * mm, "mid": v(-24.16, -7.88) * mm, "end": v(-24.4, -8.05) * mm});
            skLineSegment(sketch, "E52.9.10", {"start": v(-22.95, -10.23) * mm, "end": v(-21.61, -9.72) * mm});
            skArc(sketch, "E52.9.11", {"start": v(-25.22, -9.9) * mm, "mid": v(-25.08, -10.1) * mm, "end": v(-24.87, -10.2) * mm});
            skLineSegment(sketch, "E52.9.12", {"start": v(-25.37, -9.51) * mm, "end": v(-25.3, -9.72) * mm});
            skLineSegment(sketch, "E52.9.13", {"start": v(-25.22, -9.9) * mm, "end": v(-25.3, -9.72) * mm});
            skPoint(sketch, "E52.10.0", {"position": v(-22.46, -15.14) * mm});
            skArc(sketch, "E52.10.1", {"start": v(-22.19, -12.95) * mm, "mid": v(-22.56, -13.52) * mm, "end": v(-22.87, -14.12) * mm});
            skLineSegment(sketch, "E52.10.2", {"start": v(-21.77, -12.55) * mm, "end": v(-20.57, -11.77) * mm});
            skPoint(sketch, "E52.10.3", {"position": v(-22, -12.7) * mm});
            skPoint(sketch, "E52.10.4", {"position": v(-20.55, -14.93) * mm});
            skArc(sketch, "E52.10.5", {"start": v(-20.85, -15) * mm, "mid": v(-21.52, -15.11) * mm, "end": v(-22.2, -15.15) * mm});
            skPoint(sketch, "E52.10.6", {"position": v(-22.97, -14.36) * mm});
            skArc(sketch, "E52.10.7", {"start": v(-22.87, -14.12) * mm, "mid": v(-22.9, -14.36) * mm, "end": v(-22.84, -14.58) * mm});
            skArc(sketch, "E52.10.8", {"start": v(-20.85, -15) * mm, "mid": v(-20.58, -14.92) * mm, "end": v(-20.32, -14.78) * mm});
            skArc(sketch, "E52.10.9", {"start": v(-21.77, -12.55) * mm, "mid": v(-22, -12.73) * mm, "end": v(-22.19, -12.95) * mm});
            skLineSegment(sketch, "E52.10.10", {"start": v(-20.32, -14.78) * mm, "end": v(-19.12, -14) * mm});
            skArc(sketch, "E52.10.11", {"start": v(-22.61, -14.94) * mm, "mid": v(-22.43, -15.09) * mm, "end": v(-22.2, -15.15) * mm});
            skLineSegment(sketch, "E52.10.12", {"start": v(-22.84, -14.58) * mm, "end": v(-22.74, -14.76) * mm});
            skLineSegment(sketch, "E52.10.13", {"start": v(-22.61, -14.94) * mm, "end": v(-22.74, -14.76) * mm});
            skPoint(sketch, "E52.11.0", {"position": v(-18.83, -19.48) * mm});
            skArc(sketch, "E52.11.1", {"start": v(-19.01, -17.28) * mm, "mid": v(-19.25, -17.91) * mm, "end": v(-19.43, -18.57) * mm});
            skLineSegment(sketch, "E52.11.2", {"start": v(-18.68, -16.8) * mm, "end": v(-17.67, -15.8) * mm});
            skPoint(sketch, "E52.11.3", {"position": v(-18.88, -17) * mm});
            skPoint(sketch, "E52.11.4", {"position": v(-17, -18.88) * mm});
            skArc(sketch, "E52.11.5", {"start": v(-17.28, -19.01) * mm, "mid": v(-17.91, -19.25) * mm, "end": v(-18.57, -19.43) * mm});
            skPoint(sketch, "E52.11.6", {"position": v(-19.48, -18.83) * mm});
            skArc(sketch, "E52.11.7", {"start": v(-19.43, -18.57) * mm, "mid": v(-19.42, -18.8) * mm, "end": v(-19.31, -19.01) * mm});
            skArc(sketch, "E52.11.8", {"start": v(-17.28, -19.01) * mm, "mid": v(-17.03, -18.87) * mm, "end": v(-16.8, -18.68) * mm});
            skArc(sketch, "E52.11.9", {"start": v(-18.68, -16.8) * mm, "mid": v(-18.87, -17.03) * mm, "end": v(-19.01, -17.28) * mm});
            skLineSegment(sketch, "E52.11.10", {"start": v(-16.8, -18.68) * mm, "end": v(-15.8, -17.67) * mm});
            skArc(sketch, "E52.11.11", {"start": v(-19.01, -19.31) * mm, "mid": v(-18.8, -19.42) * mm, "end": v(-18.57, -19.43) * mm});
            skLineSegment(sketch, "E52.11.12", {"start": v(-19.31, -19.01) * mm, "end": v(-19.17, -19.17) * mm});
            skLineSegment(sketch, "E52.11.13", {"start": v(-19.01, -19.31) * mm, "end": v(-19.17, -19.17) * mm});
            skPoint(sketch, "E52.12.0", {"position": v(-14.36, -22.97) * mm});
            skArc(sketch, "E52.12.1", {"start": v(-15, -20.85) * mm, "mid": v(-15.11, -21.52) * mm, "end": v(-15.15, -22.2) * mm});
            skLineSegment(sketch, "E52.12.2", {"start": v(-14.78, -20.32) * mm, "end": v(-14, -19.12) * mm});
            skPoint(sketch, "E52.12.3", {"position": v(-14.93, -20.55) * mm});
            skPoint(sketch, "E52.12.4", {"position": v(-12.7, -22) * mm});
            skArc(sketch, "E52.12.5", {"start": v(-12.95, -22.19) * mm, "mid": v(-13.52, -22.56) * mm, "end": v(-14.12, -22.87) * mm});
            skPoint(sketch, "E52.12.6", {"position": v(-15.14, -22.46) * mm});
            skArc(sketch, "E52.12.7", {"start": v(-15.15, -22.2) * mm, "mid": v(-15.09, -22.43) * mm, "end": v(-14.94, -22.61) * mm});
            skArc(sketch, "E52.12.8", {"start": v(-12.95, -22.19) * mm, "mid": v(-12.73, -22) * mm, "end": v(-12.55, -21.77) * mm});
            skArc(sketch, "E52.12.9", {"start": v(-14.78, -20.32) * mm, "mid": v(-14.92, -20.58) * mm, "end": v(-15, -20.85) * mm});
            skLineSegment(sketch, "E52.12.10", {"start": v(-12.55, -21.77) * mm, "end": v(-11.77, -20.57) * mm});
            skArc(sketch, "E52.12.11", {"start": v(-14.58, -22.84) * mm, "mid": v(-14.36, -22.9) * mm, "end": v(-14.12, -22.87) * mm});
            skLineSegment(sketch, "E52.12.12", {"start": v(-14.94, -22.61) * mm, "end": v(-14.76, -22.74) * mm});
            skLineSegment(sketch, "E52.12.13", {"start": v(-14.58, -22.84) * mm, "end": v(-14.76, -22.74) * mm});
            skPoint(sketch, "E52.13.0", {"position": v(-9.28, -25.45) * mm});
            skArc(sketch, "E52.13.1", {"start": v(-10.34, -23.52) * mm, "mid": v(-10.3, -24.2) * mm, "end": v(-10.2, -24.87) * mm});
            skLineSegment(sketch, "E52.13.2", {"start": v(-10.23, -22.95) * mm, "end": v(-9.72, -21.61) * mm});
            skPoint(sketch, "E52.13.3", {"position": v(-10.33, -23.2) * mm});
            skPoint(sketch, "E52.13.4", {"position": v(-7.85, -24.16) * mm});
            skArc(sketch, "E52.13.5", {"start": v(-8.05, -24.4) * mm, "mid": v(-8.53, -24.88) * mm, "end": v(-9.06, -25.3) * mm});
            skPoint(sketch, "E52.13.6", {"position": v(-10.14, -25.12) * mm});
            skArc(sketch, "E52.13.7", {"start": v(-10.2, -24.87) * mm, "mid": v(-10.1, -25.08) * mm, "end": v(-9.9, -25.22) * mm});
            skArc(sketch, "E52.13.8", {"start": v(-8.05, -24.4) * mm, "mid": v(-7.88, -24.16) * mm, "end": v(-7.75, -23.9) * mm});
            skArc(sketch, "E52.13.9", {"start": v(-10.23, -22.95) * mm, "mid": v(-10.31, -23.23) * mm, "end": v(-10.34, -23.52) * mm});
            skLineSegment(sketch, "E52.13.10", {"start": v(-7.75, -23.9) * mm, "end": v(-7.24, -22.57) * mm});
            skArc(sketch, "E52.13.11", {"start": v(-9.51, -25.37) * mm, "mid": v(-9.28, -25.4) * mm, "end": v(-9.06, -25.3) * mm});
            skLineSegment(sketch, "E52.13.12", {"start": v(-9.9, -25.22) * mm, "end": v(-9.72, -25.3) * mm});
            skLineSegment(sketch, "E52.13.13", {"start": v(-9.51, -25.37) * mm, "end": v(-9.72, -25.3) * mm});
            skPoint(sketch, "E52.14.0", {"position": v(-3.78, -26.82) * mm});
            skArc(sketch, "E52.14.1", {"start": v(-5.22, -25.15) * mm, "mid": v(-5.05, -25.8) * mm, "end": v(-4.8, -26.44) * mm});
            skLineSegment(sketch, "E52.14.2", {"start": v(-5.24, -24.58) * mm, "end": v(-5.01, -23.16) * mm});
            skPoint(sketch, "E52.14.3", {"position": v(-5.28, -24.84) * mm});
            skPoint(sketch, "E52.14.4", {"position": v(-2.66, -25.26) * mm});
            skArc(sketch, "E52.14.5", {"start": v(-2.8, -25.54) * mm, "mid": v(-3.17, -26.1) * mm, "end": v(-3.6, -26.63) * mm});
            skPoint(sketch, "E52.14.6", {"position": v(-4.7, -26.68) * mm});
            skArc(sketch, "E52.14.7", {"start": v(-4.8, -26.44) * mm, "mid": v(-4.66, -26.63) * mm, "end": v(-4.45, -26.73) * mm});
            skArc(sketch, "E52.14.8", {"start": v(-2.8, -25.54) * mm, "mid": v(-2.68, -25.27) * mm, "end": v(-2.61, -25) * mm});
            skArc(sketch, "E52.14.9", {"start": v(-5.24, -24.58) * mm, "mid": v(-5.26, -24.87) * mm, "end": v(-5.22, -25.15) * mm});
            skLineSegment(sketch, "E52.14.10", {"start": v(-2.61, -25) * mm, "end": v(-2.39, -23.58) * mm});
            skArc(sketch, "E52.14.11", {"start": v(-4.03, -26.8) * mm, "mid": v(-3.8, -26.77) * mm, "end": v(-3.6, -26.63) * mm});
            skLineSegment(sketch, "E52.14.12", {"start": v(-4.45, -26.73) * mm, "end": v(-4.24, -26.78) * mm});
            skLineSegment(sketch, "E52.14.13", {"start": v(-4.03, -26.8) * mm, "end": v(-4.24, -26.78) * mm});
            skPoint(sketch, "E52.15.0", {"position": v(1.88, -27.02) * mm});
            skArc(sketch, "E52.15.1", {"start": v(0.12, -25.69) * mm, "mid": v(0.43, -26.3) * mm, "end": v(0.8, -26.86) * mm});
            skLineSegment(sketch, "E52.15.2", {"start": v(-0.01, -25.13) * mm, "end": v(-0.09, -23.7) * mm});
            skPoint(sketch, "E52.15.3", {"position": v(0, -25.4) * mm});
            skPoint(sketch, "E52.15.4", {"position": v(2.66, -25.26) * mm});
            skArc(sketch, "E52.15.5", {"start": v(2.57, -25.56) * mm, "mid": v(2.32, -26.2) * mm, "end": v(2.02, -26.8) * mm});
            skPoint(sketch, "E52.15.6", {"position": v(0.96, -27.07) * mm});
            skArc(sketch, "E52.15.7", {"start": v(0.8, -26.86) * mm, "mid": v(0.98, -27.02) * mm, "end": v(1.2, -27.07) * mm});
            skArc(sketch, "E52.15.8", {"start": v(2.57, -25.56) * mm, "mid": v(2.63, -25.28) * mm, "end": v(2.64, -25) * mm});
            skArc(sketch, "E52.15.9", {"start": v(-0.01, -25.13) * mm, "mid": v(0.03, -25.42) * mm, "end": v(0.12, -25.69) * mm});
            skLineSegment(sketch, "E52.15.10", {"start": v(2.64, -25) * mm, "end": v(2.57, -23.56) * mm});
            skArc(sketch, "E52.15.11", {"start": v(1.63, -27.05) * mm, "mid": v(1.85, -26.97) * mm, "end": v(2.02, -26.8) * mm});
            skLineSegment(sketch, "E52.15.12", {"start": v(1.2, -27.07) * mm, "end": v(1.42, -27.07) * mm});
            skLineSegment(sketch, "E52.15.13", {"start": v(1.63, -27.05) * mm, "end": v(1.42, -27.07) * mm});
            skPoint(sketch, "E52.16.0", {"position": v(7.46, -26.04) * mm});
            skArc(sketch, "E52.16.1", {"start": v(5.46, -25.1) * mm, "mid": v(5.88, -25.63) * mm, "end": v(6.37, -26.11) * mm});
            skLineSegment(sketch, "E52.16.2", {"start": v(5.21, -24.58) * mm, "end": v(4.84, -23.2) * mm});
            skPoint(sketch, "E52.16.3", {"position": v(5.28, -24.84) * mm});
            skPoint(sketch, "E52.16.4", {"position": v(7.85, -24.16) * mm});
            skArc(sketch, "E52.16.5", {"start": v(7.82, -24.47) * mm, "mid": v(7.72, -25.14) * mm, "end": v(7.54, -25.8) * mm});
            skPoint(sketch, "E52.16.6", {"position": v(6.56, -26.28) * mm});
            skArc(sketch, "E52.16.7", {"start": v(6.37, -26.11) * mm, "mid": v(6.57, -26.22) * mm, "end": v(6.8, -26.23) * mm});
            skArc(sketch, "E52.16.8", {"start": v(7.82, -24.47) * mm, "mid": v(7.83, -24.18) * mm, "end": v(7.78, -23.9) * mm});
            skArc(sketch, "E52.16.9", {"start": v(5.21, -24.58) * mm, "mid": v(5.31, -24.85) * mm, "end": v(5.46, -25.1) * mm});
            skLineSegment(sketch, "E52.16.10", {"start": v(7.78, -23.9) * mm, "end": v(7.4, -22.51) * mm});
            skArc(sketch, "E52.16.11", {"start": v(7.22, -26.12) * mm, "mid": v(7.42, -26) * mm, "end": v(7.54, -25.8) * mm});
            skLineSegment(sketch, "E52.16.12", {"start": v(6.8, -26.23) * mm, "end": v(7.02, -26.19) * mm});
            skLineSegment(sketch, "E52.16.13", {"start": v(7.22, -26.12) * mm, "end": v(7.02, -26.19) * mm});
            skPoint(sketch, "E52.17.0", {"position": v(12.7, -23.92) * mm});
            skArc(sketch, "E52.17.1", {"start": v(10.56, -23.42) * mm, "mid": v(11.08, -23.85) * mm, "end": v(11.65, -24.22) * mm});
            skLineSegment(sketch, "E52.17.2", {"start": v(10.2, -22.96) * mm, "end": v(9.56, -21.69) * mm});
            skPoint(sketch, "E52.17.3", {"position": v(10.33, -23.2) * mm});
            skPoint(sketch, "E52.17.4", {"position": v(12.7, -22) * mm});
            skArc(sketch, "E52.17.5", {"start": v(12.74, -22.3) * mm, "mid": v(12.78, -22.98) * mm, "end": v(12.74, -23.66) * mm});
            skPoint(sketch, "E52.17.6", {"position": v(11.88, -24.34) * mm});
            skArc(sketch, "E52.17.7", {"start": v(11.65, -24.22) * mm, "mid": v(11.88, -24.28) * mm, "end": v(12.11, -24.24) * mm});
            skArc(sketch, "E52.17.8", {"start": v(12.74, -22.3) * mm, "mid": v(12.68, -22.02) * mm, "end": v(12.58, -21.76) * mm});
            skArc(sketch, "E52.17.9", {"start": v(10.2, -22.96) * mm, "mid": v(10.36, -23.2) * mm, "end": v(10.56, -23.42) * mm});
            skLineSegment(sketch, "E52.17.10", {"start": v(12.58, -21.76) * mm, "end": v(11.93, -20.48) * mm});
            skArc(sketch, "E52.17.11", {"start": v(12.5, -24.05) * mm, "mid": v(12.66, -23.89) * mm, "end": v(12.74, -23.66) * mm});
            skLineSegment(sketch, "E52.17.12", {"start": v(12.11, -24.24) * mm, "end": v(12.3, -24.15) * mm});
            skLineSegment(sketch, "E52.17.13", {"start": v(12.5, -24.05) * mm, "end": v(12.3, -24.15) * mm});
            skPoint(sketch, "E52.18.0", {"position": v(17.4, -20.76) * mm});
            skArc(sketch, "E52.18.1", {"start": v(15.2, -20.71) * mm, "mid": v(15.8, -21.02) * mm, "end": v(16.44, -21.26) * mm});
            skLineSegment(sketch, "E52.18.2", {"start": v(14.76, -20.34) * mm, "end": v(13.86, -19.22) * mm});
            skPoint(sketch, "E52.18.3", {"position": v(14.93, -20.55) * mm});
            skPoint(sketch, "E52.18.4", {"position": v(17, -18.88) * mm});
            skArc(sketch, "E52.18.5", {"start": v(17.1, -19.17) * mm, "mid": v(17.28, -19.83) * mm, "end": v(17.38, -20.5) * mm});
            skPoint(sketch, "E52.18.6", {"position": v(16.69, -21.34) * mm});
            skArc(sketch, "E52.18.7", {"start": v(16.44, -21.26) * mm, "mid": v(16.67, -21.28) * mm, "end": v(16.89, -21.2) * mm});
            skArc(sketch, "E52.18.8", {"start": v(17.1, -19.17) * mm, "mid": v(16.99, -18.9) * mm, "end": v(16.83, -18.67) * mm});
            skArc(sketch, "E52.18.9", {"start": v(14.76, -20.34) * mm, "mid": v(14.96, -20.55) * mm, "end": v(15.2, -20.71) * mm});
            skLineSegment(sketch, "E52.18.10", {"start": v(16.83, -18.67) * mm, "end": v(15.92, -17.55) * mm});
            skArc(sketch, "E52.18.11", {"start": v(17.22, -20.93) * mm, "mid": v(17.35, -20.73) * mm, "end": v(17.38, -20.5) * mm});
            skLineSegment(sketch, "E52.18.12", {"start": v(16.89, -21.2) * mm, "end": v(17.06, -21.07) * mm});
            skLineSegment(sketch, "E52.18.13", {"start": v(17.22, -20.93) * mm, "end": v(17.06, -21.07) * mm});
            skPoint(sketch, "E52.19.0", {"position": v(21.34, -16.69) * mm});
            skArc(sketch, "E52.19.1", {"start": v(19.17, -17.1) * mm, "mid": v(19.83, -17.28) * mm, "end": v(20.5, -17.38) * mm});
            skLineSegment(sketch, "E52.19.2", {"start": v(18.67, -16.83) * mm, "end": v(17.55, -15.92) * mm});
            skPoint(sketch, "E52.19.3", {"position": v(18.88, -17) * mm});
            skPoint(sketch, "E52.19.4", {"position": v(20.55, -14.93) * mm});
            skArc(sketch, "E52.19.5", {"start": v(20.71, -15.2) * mm, "mid": v(21.02, -15.8) * mm, "end": v(21.26, -16.44) * mm});
            skPoint(sketch, "E52.19.6", {"position": v(20.76, -17.4) * mm});
            skArc(sketch, "E52.19.7", {"start": v(20.5, -17.38) * mm, "mid": v(20.73, -17.35) * mm, "end": v(20.93, -17.22) * mm});
            skArc(sketch, "E52.19.8", {"start": v(20.71, -15.2) * mm, "mid": v(20.55, -14.96) * mm, "end": v(20.34, -14.76) * mm});
            skArc(sketch, "E52.19.9", {"start": v(18.67, -16.83) * mm, "mid": v(18.9, -16.99) * mm, "end": v(19.17, -17.1) * mm});
            skLineSegment(sketch, "E52.19.10", {"start": v(20.34, -14.76) * mm, "end": v(19.22, -13.86) * mm});
            skArc(sketch, "E52.19.11", {"start": v(21.2, -16.89) * mm, "mid": v(21.28, -16.67) * mm, "end": v(21.26, -16.44) * mm});
            skLineSegment(sketch, "E52.19.12", {"start": v(20.93, -17.22) * mm, "end": v(21.07, -17.06) * mm});
            skLineSegment(sketch, "E52.19.13", {"start": v(21.2, -16.89) * mm, "end": v(21.07, -17.06) * mm});
            skPoint(sketch, "E52.20.0", {"position": v(24.34, -11.88) * mm});
            skArc(sketch, "E52.20.1", {"start": v(22.3, -12.74) * mm, "mid": v(22.98, -12.78) * mm, "end": v(23.66, -12.74) * mm});
            skLineSegment(sketch, "E52.20.2", {"start": v(21.76, -12.58) * mm, "end": v(20.48, -11.93) * mm});
            skPoint(sketch, "E52.20.3", {"position": v(22, -12.7) * mm});
            skPoint(sketch, "E52.20.4", {"position": v(23.2, -10.33) * mm});
            skArc(sketch, "E52.20.5", {"start": v(23.42, -10.56) * mm, "mid": v(23.85, -11.08) * mm, "end": v(24.22, -11.65) * mm});
            skPoint(sketch, "E52.20.6", {"position": v(23.92, -12.7) * mm});
            skArc(sketch, "E52.20.7", {"start": v(23.66, -12.74) * mm, "mid": v(23.89, -12.66) * mm, "end": v(24.05, -12.5) * mm});
            skArc(sketch, "E52.20.8", {"start": v(23.42, -10.56) * mm, "mid": v(23.2, -10.36) * mm, "end": v(22.96, -10.2) * mm});
            skArc(sketch, "E52.20.9", {"start": v(21.76, -12.58) * mm, "mid": v(22.02, -12.68) * mm, "end": v(22.3, -12.74) * mm});
            skLineSegment(sketch, "E52.20.10", {"start": v(22.96, -10.2) * mm, "end": v(21.69, -9.56) * mm});
            skArc(sketch, "E52.20.11", {"start": v(24.24, -12.11) * mm, "mid": v(24.28, -11.88) * mm, "end": v(24.22, -11.65) * mm});
            skLineSegment(sketch, "E52.20.12", {"start": v(24.05, -12.5) * mm, "end": v(24.15, -12.3) * mm});
            skLineSegment(sketch, "E52.20.13", {"start": v(24.24, -12.11) * mm, "end": v(24.15, -12.3) * mm});
            skPoint(sketch, "E52.21.0", {"position": v(26.28, -6.56) * mm});
            skArc(sketch, "E52.21.1", {"start": v(24.47, -7.82) * mm, "mid": v(25.14, -7.72) * mm, "end": v(25.8, -7.54) * mm});
            skLineSegment(sketch, "E52.21.2", {"start": v(23.9, -7.78) * mm, "end": v(22.51, -7.4) * mm});
            skPoint(sketch, "E52.21.3", {"position": v(24.16, -7.85) * mm});
            skPoint(sketch, "E52.21.4", {"position": v(24.84, -5.28) * mm});
            skArc(sketch, "E52.21.5", {"start": v(25.1, -5.46) * mm, "mid": v(25.63, -5.88) * mm, "end": v(26.11, -6.37) * mm});
            skPoint(sketch, "E52.21.6", {"position": v(26.04, -7.46) * mm});
            skArc(sketch, "E52.21.7", {"start": v(25.8, -7.54) * mm, "mid": v(26, -7.42) * mm, "end": v(26.12, -7.22) * mm});
            skArc(sketch, "E52.21.8", {"start": v(25.1, -5.46) * mm, "mid": v(24.85, -5.31) * mm, "end": v(24.58, -5.21) * mm});
            skArc(sketch, "E52.21.9", {"start": v(23.9, -7.78) * mm, "mid": v(24.18, -7.83) * mm, "end": v(24.47, -7.82) * mm});
            skLineSegment(sketch, "E52.21.10", {"start": v(24.58, -5.21) * mm, "end": v(23.2, -4.84) * mm});
            skArc(sketch, "E52.21.11", {"start": v(26.23, -6.8) * mm, "mid": v(26.22, -6.57) * mm, "end": v(26.11, -6.37) * mm});
            skLineSegment(sketch, "E52.21.12", {"start": v(26.12, -7.22) * mm, "end": v(26.19, -7.02) * mm});
            skLineSegment(sketch, "E52.21.13", {"start": v(26.23, -6.8) * mm, "end": v(26.19, -7.02) * mm});
            skPoint(sketch, "E52.22.0", {"position": v(27.07, -0.96) * mm});
            skArc(sketch, "E52.22.1", {"start": v(25.56, -2.57) * mm, "mid": v(26.2, -2.32) * mm, "end": v(26.8, -2.02) * mm});
            skLineSegment(sketch, "E52.22.2", {"start": v(25, -2.64) * mm, "end": v(23.56, -2.57) * mm});
            skPoint(sketch, "E52.22.3", {"position": v(25.26, -2.66) * mm});
            skPoint(sketch, "E52.22.4", {"position": v(25.4, 0) * mm});
            skArc(sketch, "E52.22.5", {"start": v(25.69, -0.12) * mm, "mid": v(26.3, -0.43) * mm, "end": v(26.86, -0.8) * mm});
            skPoint(sketch, "E52.22.6", {"position": v(27.02, -1.88) * mm});
            skArc(sketch, "E52.22.7", {"start": v(26.8, -2.02) * mm, "mid": v(26.97, -1.85) * mm, "end": v(27.05, -1.63) * mm});
            skArc(sketch, "E52.22.8", {"start": v(25.69, -0.12) * mm, "mid": v(25.42, -0.03) * mm, "end": v(25.13, 0.01) * mm});
            skArc(sketch, "E52.22.9", {"start": v(25, -2.64) * mm, "mid": v(25.28, -2.63) * mm, "end": v(25.56, -2.57) * mm});
            skLineSegment(sketch, "E52.22.10", {"start": v(25.13, 0.01) * mm, "end": v(23.7, 0.09) * mm});
            skArc(sketch, "E52.22.11", {"start": v(27.07, -1.2) * mm, "mid": v(27.02, -0.98) * mm, "end": v(26.86, -0.8) * mm});
            skLineSegment(sketch, "E52.22.12", {"start": v(27.05, -1.63) * mm, "end": v(27.07, -1.42) * mm});
            skLineSegment(sketch, "E52.22.13", {"start": v(27.07, -1.2) * mm, "end": v(27.07, -1.42) * mm});
            skPoint(sketch, "E52.23.0", {"position": v(26.68, 4.7) * mm});
            skArc(sketch, "E52.23.1", {"start": v(25.54, 2.8) * mm, "mid": v(26.1, 3.17) * mm, "end": v(26.63, 3.6) * mm});
            skLineSegment(sketch, "E52.23.2", {"start": v(25, 2.61) * mm, "end": v(23.58, 2.39) * mm});
            skPoint(sketch, "E52.23.3", {"position": v(25.26, 2.66) * mm});
            skPoint(sketch, "E52.23.4", {"position": v(24.84, 5.28) * mm});
            skArc(sketch, "E52.23.5", {"start": v(25.15, 5.22) * mm, "mid": v(25.8, 5.05) * mm, "end": v(26.44, 4.8) * mm});
            skPoint(sketch, "E52.23.6", {"position": v(26.82, 3.78) * mm});
            skArc(sketch, "E52.23.7", {"start": v(26.63, 3.6) * mm, "mid": v(26.77, 3.8) * mm, "end": v(26.8, 4.03) * mm});
            skArc(sketch, "E52.23.8", {"start": v(25.15, 5.22) * mm, "mid": v(24.87, 5.26) * mm, "end": v(24.58, 5.24) * mm});
            skArc(sketch, "E52.23.9", {"start": v(25, 2.61) * mm, "mid": v(25.27, 2.68) * mm, "end": v(25.54, 2.8) * mm});
            skLineSegment(sketch, "E52.23.10", {"start": v(24.58, 5.24) * mm, "end": v(23.16, 5.01) * mm});
            skArc(sketch, "E52.23.11", {"start": v(26.73, 4.45) * mm, "mid": v(26.63, 4.66) * mm, "end": v(26.44, 4.8) * mm});
            skLineSegment(sketch, "E52.23.12", {"start": v(26.8, 4.03) * mm, "end": v(26.78, 4.24) * mm});
            skLineSegment(sketch, "E52.23.13", {"start": v(26.73, 4.45) * mm, "end": v(26.78, 4.24) * mm});
            skPoint(sketch, "E52.24.0", {"position": v(25.12, 10.14) * mm});
            skArc(sketch, "E52.24.1", {"start": v(24.4, 8.05) * mm, "mid": v(24.88, 8.53) * mm, "end": v(25.3, 9.06) * mm});
            skLineSegment(sketch, "E52.24.2", {"start": v(23.9, 7.75) * mm, "end": v(22.57, 7.24) * mm});
            skPoint(sketch, "E52.24.3", {"position": v(24.16, 7.85) * mm});
            skPoint(sketch, "E52.24.4", {"position": v(23.2, 10.33) * mm});
            skArc(sketch, "E52.24.5", {"start": v(23.52, 10.34) * mm, "mid": v(24.2, 10.3) * mm, "end": v(24.87, 10.2) * mm});
            skPoint(sketch, "E52.24.6", {"position": v(25.45, 9.28) * mm});
            skArc(sketch, "E52.24.7", {"start": v(25.3, 9.06) * mm, "mid": v(25.4, 9.28) * mm, "end": v(25.37, 9.51) * mm});
            skArc(sketch, "E52.24.8", {"start": v(23.52, 10.34) * mm, "mid": v(23.23, 10.31) * mm, "end": v(22.95, 10.23) * mm});
            skArc(sketch, "E52.24.9", {"start": v(23.9, 7.75) * mm, "mid": v(24.16, 7.88) * mm, "end": v(24.4, 8.05) * mm});
            skLineSegment(sketch, "E52.24.10", {"start": v(22.95, 10.23) * mm, "end": v(21.61, 9.72) * mm});
            skArc(sketch, "E52.24.11", {"start": v(25.22, 9.9) * mm, "mid": v(25.08, 10.1) * mm, "end": v(24.87, 10.2) * mm});
            skLineSegment(sketch, "E52.24.12", {"start": v(25.37, 9.51) * mm, "end": v(25.3, 9.72) * mm});
            skLineSegment(sketch, "E52.24.13", {"start": v(25.22, 9.9) * mm, "end": v(25.3, 9.72) * mm});
            skPoint(sketch, "E52.25.0", {"position": v(22.46, 15.14) * mm});
            skArc(sketch, "E52.25.1", {"start": v(22.19, 12.95) * mm, "mid": v(22.56, 13.52) * mm, "end": v(22.87, 14.12) * mm});
            skLineSegment(sketch, "E52.25.2", {"start": v(21.77, 12.55) * mm, "end": v(20.57, 11.77) * mm});
            skPoint(sketch, "E52.25.3", {"position": v(22, 12.7) * mm});
            skPoint(sketch, "E52.25.4", {"position": v(20.55, 14.93) * mm});
            skArc(sketch, "E52.25.5", {"start": v(20.85, 15) * mm, "mid": v(21.52, 15.11) * mm, "end": v(22.2, 15.15) * mm});
            skPoint(sketch, "E52.25.6", {"position": v(22.97, 14.36) * mm});
            skArc(sketch, "E52.25.7", {"start": v(22.87, 14.12) * mm, "mid": v(22.9, 14.36) * mm, "end": v(22.84, 14.58) * mm});
            skArc(sketch, "E52.25.8", {"start": v(20.85, 15) * mm, "mid": v(20.58, 14.92) * mm, "end": v(20.32, 14.78) * mm});
            skArc(sketch, "E52.25.9", {"start": v(21.77, 12.55) * mm, "mid": v(22, 12.73) * mm, "end": v(22.19, 12.95) * mm});
            skLineSegment(sketch, "E52.25.10", {"start": v(20.32, 14.78) * mm, "end": v(19.12, 14) * mm});
            skArc(sketch, "E52.25.11", {"start": v(22.61, 14.94) * mm, "mid": v(22.43, 15.09) * mm, "end": v(22.2, 15.15) * mm});
            skLineSegment(sketch, "E52.25.12", {"start": v(22.84, 14.58) * mm, "end": v(22.74, 14.76) * mm});
            skLineSegment(sketch, "E52.25.13", {"start": v(22.61, 14.94) * mm, "end": v(22.74, 14.76) * mm});
            skPoint(sketch, "E52.26.0", {"position": v(18.83, 19.48) * mm});
            skArc(sketch, "E52.26.1", {"start": v(19.01, 17.28) * mm, "mid": v(19.25, 17.91) * mm, "end": v(19.43, 18.57) * mm});
            skLineSegment(sketch, "E52.26.2", {"start": v(18.68, 16.8) * mm, "end": v(17.67, 15.8) * mm});
            skPoint(sketch, "E52.26.3", {"position": v(18.88, 17) * mm});
            skPoint(sketch, "E52.26.4", {"position": v(17, 18.88) * mm});
            skArc(sketch, "E52.26.5", {"start": v(17.28, 19.01) * mm, "mid": v(17.91, 19.25) * mm, "end": v(18.57, 19.43) * mm});
            skPoint(sketch, "E52.26.6", {"position": v(19.48, 18.83) * mm});
            skArc(sketch, "E52.26.7", {"start": v(19.43, 18.57) * mm, "mid": v(19.42, 18.8) * mm, "end": v(19.31, 19.01) * mm});
            skArc(sketch, "E52.26.8", {"start": v(17.28, 19.01) * mm, "mid": v(17.03, 18.87) * mm, "end": v(16.8, 18.68) * mm});
            skArc(sketch, "E52.26.9", {"start": v(18.68, 16.8) * mm, "mid": v(18.87, 17.03) * mm, "end": v(19.01, 17.28) * mm});
            skLineSegment(sketch, "E52.26.10", {"start": v(16.8, 18.68) * mm, "end": v(15.8, 17.67) * mm});
            skArc(sketch, "E52.26.11", {"start": v(19.01, 19.31) * mm, "mid": v(18.8, 19.42) * mm, "end": v(18.57, 19.43) * mm});
            skLineSegment(sketch, "E52.26.12", {"start": v(19.31, 19.01) * mm, "end": v(19.17, 19.17) * mm});
            skLineSegment(sketch, "E52.26.13", {"start": v(19.01, 19.31) * mm, "end": v(19.17, 19.17) * mm});
            skPoint(sketch, "E52.27.0", {"position": v(14.36, 22.97) * mm});
            skArc(sketch, "E52.27.1", {"start": v(15, 20.85) * mm, "mid": v(15.11, 21.52) * mm, "end": v(15.15, 22.2) * mm});
            skLineSegment(sketch, "E52.27.2", {"start": v(14.78, 20.32) * mm, "end": v(14, 19.12) * mm});
            skPoint(sketch, "E52.27.3", {"position": v(14.93, 20.55) * mm});
            skPoint(sketch, "E52.27.4", {"position": v(12.7, 22) * mm});
            skArc(sketch, "E52.27.5", {"start": v(12.95, 22.19) * mm, "mid": v(13.52, 22.56) * mm, "end": v(14.12, 22.87) * mm});
            skPoint(sketch, "E52.27.6", {"position": v(15.14, 22.46) * mm});
            skArc(sketch, "E52.27.7", {"start": v(15.15, 22.2) * mm, "mid": v(15.09, 22.43) * mm, "end": v(14.94, 22.61) * mm});
            skArc(sketch, "E52.27.8", {"start": v(12.95, 22.19) * mm, "mid": v(12.73, 22) * mm, "end": v(12.55, 21.77) * mm});
            skArc(sketch, "E52.27.9", {"start": v(14.78, 20.32) * mm, "mid": v(14.92, 20.58) * mm, "end": v(15, 20.85) * mm});
            skLineSegment(sketch, "E52.27.10", {"start": v(12.55, 21.77) * mm, "end": v(11.77, 20.57) * mm});
            skArc(sketch, "E52.27.11", {"start": v(14.58, 22.84) * mm, "mid": v(14.36, 22.9) * mm, "end": v(14.12, 22.87) * mm});
            skLineSegment(sketch, "E52.27.12", {"start": v(14.94, 22.61) * mm, "end": v(14.76, 22.74) * mm});
            skLineSegment(sketch, "E52.27.13", {"start": v(14.58, 22.84) * mm, "end": v(14.76, 22.74) * mm});
            skPoint(sketch, "E52.28.0", {"position": v(9.28, 25.45) * mm});
            skArc(sketch, "E52.28.1", {"start": v(10.34, 23.52) * mm, "mid": v(10.3, 24.2) * mm, "end": v(10.2, 24.87) * mm});
            skLineSegment(sketch, "E52.28.2", {"start": v(10.23, 22.95) * mm, "end": v(9.72, 21.61) * mm});
            skPoint(sketch, "E52.28.3", {"position": v(10.33, 23.2) * mm});
            skPoint(sketch, "E52.28.4", {"position": v(7.85, 24.16) * mm});
            skArc(sketch, "E52.28.5", {"start": v(8.05, 24.4) * mm, "mid": v(8.53, 24.88) * mm, "end": v(9.06, 25.3) * mm});
            skPoint(sketch, "E52.28.6", {"position": v(10.14, 25.12) * mm});
            skArc(sketch, "E52.28.7", {"start": v(10.2, 24.87) * mm, "mid": v(10.1, 25.08) * mm, "end": v(9.9, 25.22) * mm});
            skArc(sketch, "E52.28.8", {"start": v(8.05, 24.4) * mm, "mid": v(7.88, 24.16) * mm, "end": v(7.75, 23.9) * mm});
            skArc(sketch, "E52.28.9", {"start": v(10.23, 22.95) * mm, "mid": v(10.31, 23.23) * mm, "end": v(10.34, 23.52) * mm});
            skLineSegment(sketch, "E52.28.10", {"start": v(7.75, 23.9) * mm, "end": v(7.24, 22.57) * mm});
            skArc(sketch, "E52.28.11", {"start": v(9.51, 25.37) * mm, "mid": v(9.28, 25.4) * mm, "end": v(9.06, 25.3) * mm});
            skLineSegment(sketch, "E52.28.12", {"start": v(9.9, 25.22) * mm, "end": v(9.72, 25.3) * mm});
            skLineSegment(sketch, "E52.28.13", {"start": v(9.51, 25.37) * mm, "end": v(9.72, 25.3) * mm});
            skPoint(sketch, "E52.29.0", {"position": v(3.78, 26.82) * mm});
            skArc(sketch, "E52.29.1", {"start": v(5.22, 25.15) * mm, "mid": v(5.05, 25.8) * mm, "end": v(4.8, 26.44) * mm});
            skLineSegment(sketch, "E52.29.2", {"start": v(5.24, 24.58) * mm, "end": v(5.01, 23.16) * mm});
            skPoint(sketch, "E52.29.3", {"position": v(5.28, 24.84) * mm});
            skPoint(sketch, "E52.29.4", {"position": v(2.66, 25.26) * mm});
            skArc(sketch, "E52.29.5", {"start": v(2.8, 25.54) * mm, "mid": v(3.17, 26.1) * mm, "end": v(3.6, 26.63) * mm});
            skPoint(sketch, "E52.29.6", {"position": v(4.7, 26.68) * mm});
            skArc(sketch, "E52.29.7", {"start": v(4.8, 26.44) * mm, "mid": v(4.66, 26.63) * mm, "end": v(4.45, 26.73) * mm});
            skArc(sketch, "E52.29.8", {"start": v(2.8, 25.54) * mm, "mid": v(2.68, 25.27) * mm, "end": v(2.61, 25) * mm});
            skArc(sketch, "E52.29.9", {"start": v(5.24, 24.58) * mm, "mid": v(5.26, 24.87) * mm, "end": v(5.22, 25.15) * mm});
            skLineSegment(sketch, "E52.29.10", {"start": v(2.61, 25) * mm, "end": v(2.39, 23.58) * mm});
            skArc(sketch, "E52.29.11", {"start": v(4.03, 26.8) * mm, "mid": v(3.8, 26.77) * mm, "end": v(3.6, 26.63) * mm});
            skLineSegment(sketch, "E52.29.12", {"start": v(4.45, 26.73) * mm, "end": v(4.24, 26.78) * mm});
            skLineSegment(sketch, "E52.29.13", {"start": v(4.03, 26.8) * mm, "end": v(4.24, 26.78) * mm});
            skArc(sketch, "E53.trimOffspring", {"start": v(-7.4, 22.51) * mm, "mid": v(-8.5, 22.12) * mm, "end": v(-9.56, 21.69) * mm});
            skArc(sketch, "E54.trimOffspring", {"start": v(-11.93, 20.48) * mm, "mid": v(-12.9, 19.87) * mm, "end": v(-13.86, 19.22) * mm});
            skArc(sketch, "E55.trimOffspring", {"start": v(-15.92, 17.55) * mm, "mid": v(-16.76, 16.76) * mm, "end": v(-17.55, 15.92) * mm});
            skArc(sketch, "E56.trimOffspring", {"start": v(-19.22, 13.86) * mm, "mid": v(-19.87, 12.9) * mm, "end": v(-20.48, 11.93) * mm});
            skArc(sketch, "E57.trimOffspring", {"start": v(-21.69, 9.56) * mm, "mid": v(-22.12, 8.5) * mm, "end": v(-22.51, 7.4) * mm});
            skArc(sketch, "E58.trimOffspring", {"start": v(-23.2, 4.84) * mm, "mid": v(-23.4, 3.7) * mm, "end": v(-23.56, 2.57) * mm});
            skArc(sketch, "E59.trimOffspring", {"start": v(-23.7, -0.09) * mm, "mid": v(-23.67, -1.24) * mm, "end": v(-23.58, -2.39) * mm});
            skArc(sketch, "E60.trimOffspring", {"start": v(-23.16, -5.01) * mm, "mid": v(-22.9, -6.13) * mm, "end": v(-22.57, -7.24) * mm});
            skArc(sketch, "E61.trimOffspring", {"start": v(-21.61, -9.72) * mm, "mid": v(-21.12, -10.76) * mm, "end": v(-20.57, -11.77) * mm});
            skArc(sketch, "E62.trimOffspring", {"start": v(-19.12, -14) * mm, "mid": v(-18.42, -14.91) * mm, "end": v(-17.67, -15.8) * mm});
            skArc(sketch, "E63.trimOffspring", {"start": v(-15.8, -17.67) * mm, "mid": v(-14.91, -18.42) * mm, "end": v(-14, -19.12) * mm});
            skArc(sketch, "E64.trimOffspring", {"start": v(-11.77, -20.57) * mm, "mid": v(-10.76, -21.12) * mm, "end": v(-9.72, -21.61) * mm});
            skArc(sketch, "E65.trimOffspring", {"start": v(-7.24, -22.57) * mm, "mid": v(-6.13, -22.9) * mm, "end": v(-5.01, -23.16) * mm});
            skArc(sketch, "E66.trimOffspring", {"start": v(-2.39, -23.58) * mm, "mid": v(-1.24, -23.67) * mm, "end": v(-0.09, -23.7) * mm});
            skArc(sketch, "E67.trimOffspring", {"start": v(2.57, -23.56) * mm, "mid": v(3.7, -23.4) * mm, "end": v(4.84, -23.2) * mm});
            skArc(sketch, "E68.trimOffspring", {"start": v(7.4, -22.51) * mm, "mid": v(8.5, -22.12) * mm, "end": v(9.56, -21.69) * mm});
            skArc(sketch, "E69.trimOffspring", {"start": v(11.93, -20.48) * mm, "mid": v(12.9, -19.87) * mm, "end": v(13.86, -19.22) * mm});
            skArc(sketch, "E70.trimOffspring", {"start": v(15.92, -17.55) * mm, "mid": v(16.76, -16.76) * mm, "end": v(17.55, -15.92) * mm});
            skArc(sketch, "E71.trimOffspring", {"start": v(19.22, -13.86) * mm, "mid": v(19.87, -12.9) * mm, "end": v(20.48, -11.93) * mm});
            skArc(sketch, "E72.trimOffspring", {"start": v(21.69, -9.56) * mm, "mid": v(22.12, -8.5) * mm, "end": v(22.51, -7.4) * mm});
            skArc(sketch, "E73.trimOffspring", {"start": v(23.2, -4.84) * mm, "mid": v(23.4, -3.7) * mm, "end": v(23.56, -2.57) * mm});
            skArc(sketch, "E74.trimOffspring", {"start": v(23.7, 0.09) * mm, "mid": v(23.67, 1.24) * mm, "end": v(23.58, 2.39) * mm});
            skArc(sketch, "E75.trimOffspring", {"start": v(23.16, 5.01) * mm, "mid": v(22.9, 6.13) * mm, "end": v(22.57, 7.24) * mm});
            skArc(sketch, "E76.trimOffspring", {"start": v(21.61, 9.72) * mm, "mid": v(21.12, 10.76) * mm, "end": v(20.57, 11.77) * mm});
            skArc(sketch, "E77.trimOffspring", {"start": v(19.12, 14) * mm, "mid": v(18.42, 14.91) * mm, "end": v(17.67, 15.8) * mm});
            skArc(sketch, "E78.trimOffspring", {"start": v(15.8, 17.67) * mm, "mid": v(14.91, 18.42) * mm, "end": v(14, 19.12) * mm});
            skArc(sketch, "E79.trimOffspring", {"start": v(11.77, 20.57) * mm, "mid": v(10.76, 21.12) * mm, "end": v(9.72, 21.61) * mm});
            skArc(sketch, "E80.trimOffspring", {"start": v(7.24, 22.57) * mm, "mid": v(6.13, 22.9) * mm, "end": v(5.01, 23.16) * mm});
            skArc(sketch, "E81.trimOffspring", {"start": v(2.39, 23.58) * mm, "mid": v(1.24, 23.67) * mm, "end": v(0.09, 23.7) * mm});
            skSolve(sketch);
        }
        {
            var Q0;
            Q0 = qSketchRegion(id + "F2", true);
            var Q1;
            Q1 = qSketchRegion(id + "F1", true);
            var Q2;
            Q2=sQuery(id+"F2.wireOp",VERTEX,"E43.end");
            var Q3;
            Q3=sQuery(id+"F1.wireOp",VERTEX,"E39.trimOffspring.end");
            loft(context, id + "F3", {"sheetProfilesArray" : [{ "sheetProfileEntities" : qUnion([Q0]) }, { "sheetProfileEntities" : qUnion([Q1]) }], "matchConnections" : true, "connections" : [{ "connectionEntities" : qUnion([Q2, Q3]), "connectionEdgeQueries" : qUnion([]), "connectionEdgeParameters" : [] }]});
        }
        {
            var Q0;
            Q0=sQuery(id+"F1.wireOp",VERTEX,"E0.center");
            var Q1;
            Q1=makeQuery(id+"F3.opLoft","SWEPT_BODY",BODY,{"disambiguationData":[OSD([makeQuery(id+"F1.imprint","IMPRINT",FACE,{"disambiguationData":[TD([[makeQuery(id+"F1.imprint","IMPRINT",EDGE,{"derivedFrom":sQuery(id+"F1.wireOp",EDGE,"E0")}),1.0]])]}),makeQuery(id+"F2.imprint","IMPRINT",FACE,{"disambiguationData":[TD([[makeQuery(id+"F2.imprint","IMPRINT",EDGE,{"derivedFrom":sQuery(id+"F2.wireOp",EDGE,"E41")}),1.0]])]})])]});
            hole(context, id + "F4", {"style" : HoleStyle.SIMPLE, "endStyle" : HoleEndStyle.BLIND, "oppositeDirection" : true, "holeDiameter" : 12.7 * mm, "holeDepth" : 50.8 * mm, "tappedDepth" : 12.7 * mm, "tapClearance" : 3, "locations" : qUnion([Q0]), "scope" : qUnion([Q1])});
        }
    });
